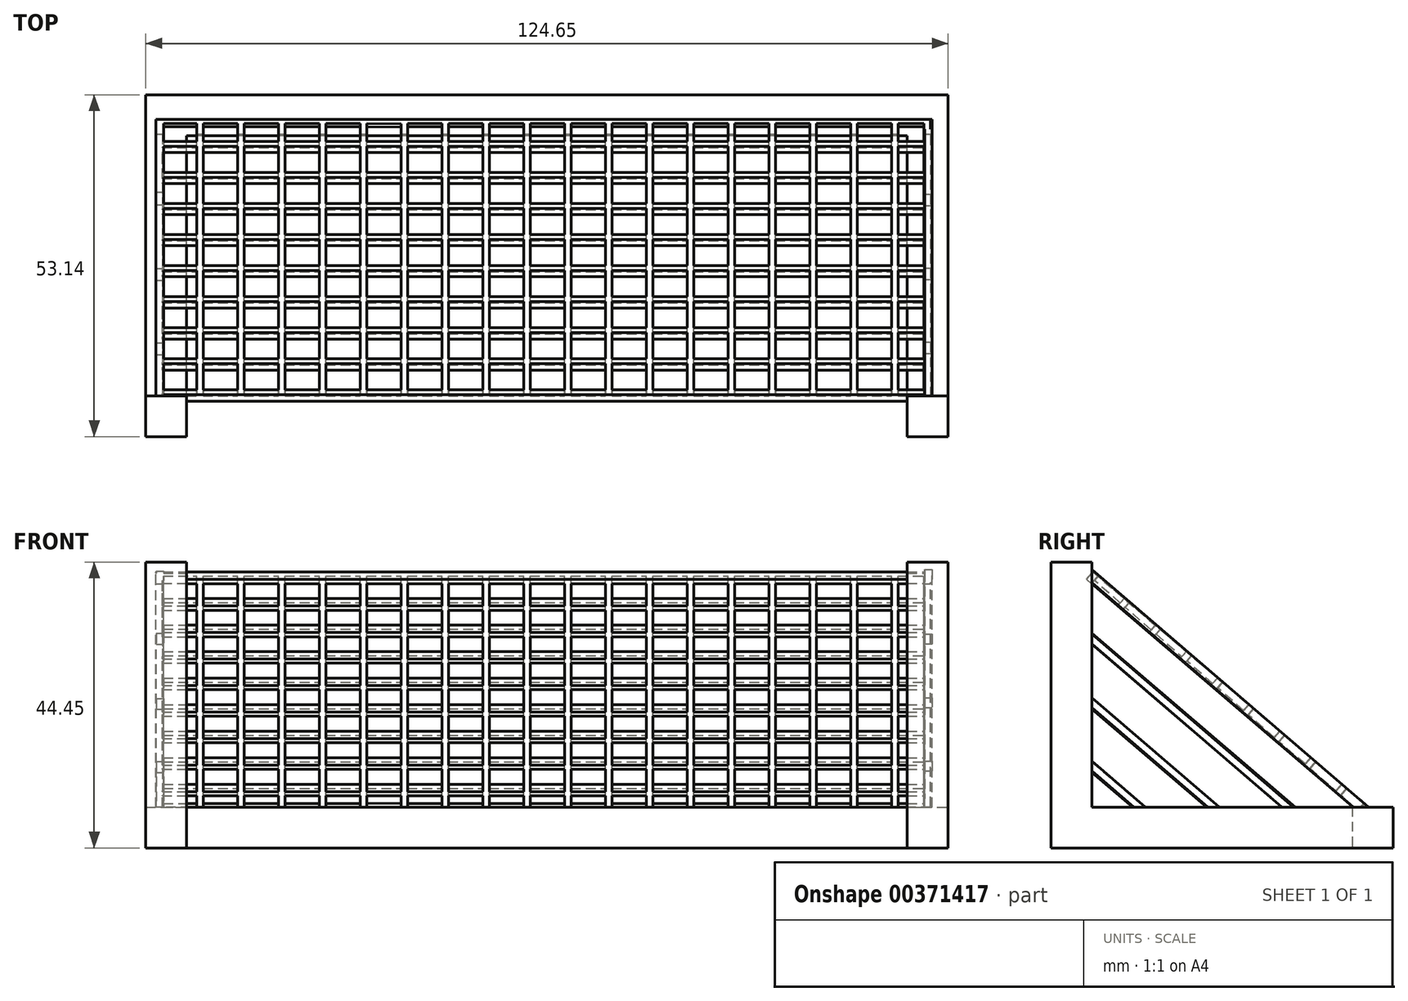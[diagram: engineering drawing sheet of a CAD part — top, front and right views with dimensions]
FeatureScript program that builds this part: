
annotation { "Feature Type Name" : "Feature", "Feature Type Description" : "" }
export const myFeature = defineFeature(function(context is Context, id is Id, definition is map)
    precondition{}
    {
        {
            var Q0;
            Q0=qCreatedBy(makeId("Top.planeOp"),FACE);
            var sketch = newSketch(context, id + "F0", { "sketchPlane" : qUnion([Q0])});
            skLineSegment(sketch, "E0.top", {"start": v(50.52, 38) * mm, "end": v(-74.13, 38) * mm});
            skLineSegment(sketch, "E0.left", {"start": v(50.52, -15.13) * mm, "end": v(50.52, 38) * mm});
            skLineSegment(sketch, "E0.right", {"start": v(-74.13, -15.13) * mm, "end": v(-74.13, 38) * mm});
            skPoint(sketch, "E0.middle", {"position": v(-11.8, 8.26) * mm});
            skLineSegment(sketch, "E1.0", {"start": v(44.17, 31.66) * mm, "end": v(-67.78, 31.66) * mm});
            skLineSegment(sketch, "E1.1", {"start": v(44.17, -15.13) * mm, "end": v(44.17, 31.66) * mm});
            skLineSegment(sketch, "E1.3", {"start": v(-67.78, -15.13) * mm, "end": v(-67.78, 31.66) * mm});
            skLineSegment(sketch, "E2", {"start": v(-74.13, -15.13) * mm, "end": v(-67.78, -15.13) * mm});
            skLineSegment(sketch, "E3", {"start": v(44.17, -15.13) * mm, "end": v(50.52, -15.13) * mm});
            skPoint(sketch, "E4.orphan", {"position": v(-74.13, -21.48) * mm});
            skPoint(sketch, "E5.orphan", {"position": v(50.52, -21.48) * mm});
            skSolve(sketch);
        }
        {
            var Q0;
            Q0=makeQuery(id+"F0.imprint","IMPRINT",FACE,{"disambiguationData":[TD([[makeQuery(id+"F0.imprint","IMPRINT",EDGE,{"derivedFrom":sQuery(id+"F0.wireOp",EDGE,"E0.top")}),1.0]])]});
            extrude(context, id + "F1", {"entities" : qUnion([Q0]), "depth" : 6.35 * mm});
        }
        {
            var Q0;
            Q0=makeQuery(id+"F1.opExtrude","CAP_FACE",FACE,{"disambiguationData":[OSD([sQuery(id+"F0.wireOp",EDGE,"E0.top"),sQuery(id+"F0.wireOp",EDGE,"E0.left"),sQuery(id+"F0.wireOp",EDGE,"E0.right"),sQuery(id+"F0.wireOp",EDGE,"E1.0"),sQuery(id+"F0.wireOp",EDGE,"E1.1"),sQuery(id+"F0.wireOp",EDGE,"E1.3"),sQuery(id+"F0.wireOp",EDGE,"E2"),sQuery(id+"F0.wireOp",EDGE,"E3")])],"isStart":false});
            var sketch = newSketch(context, id + "F2", { "sketchPlane" : qUnion([Q0])});
            skLineSegment(sketch, "E6.bottom", {"start": v(-74.13, -8.78) * mm, "end": v(-67.78, -8.78) * mm});
            skLineSegment(sketch, "E6.top", {"start": v(-74.13, -15.13) * mm, "end": v(-67.78, -15.13) * mm});
            skLineSegment(sketch, "E6.left", {"start": v(-74.13, -8.78) * mm, "end": v(-74.13, -15.13) * mm});
            skLineSegment(sketch, "E6.right", {"start": v(-67.78, -8.78) * mm, "end": v(-67.78, -15.13) * mm});
            skLineSegment(sketch, "E7.bottom", {"start": v(44.17, -8.78) * mm, "end": v(50.52, -8.78) * mm});
            skLineSegment(sketch, "E7.top", {"start": v(44.17, -15.13) * mm, "end": v(50.52, -15.13) * mm});
            skLineSegment(sketch, "E7.left", {"start": v(44.17, -8.78) * mm, "end": v(44.17, -15.13) * mm});
            skLineSegment(sketch, "E7.right", {"start": v(50.52, -8.78) * mm, "end": v(50.52, -15.13) * mm});
            skSolve(sketch);
        }
        {
            var Q0;
            Q0=makeQuery(id+"F2.imprint","IMPRINT",FACE,{"disambiguationData":[TD([[makeQuery(id+"F2.imprint","IMPRINT",EDGE,{"derivedFrom":sQuery(id+"F2.wireOp",EDGE,"E6.bottom")}),-1.0]])]});
            var Q1;
            Q1=makeQuery(id+"F2.imprint","IMPRINT",FACE,{"disambiguationData":[TD([[makeQuery(id+"F2.imprint","IMPRINT",EDGE,{"derivedFrom":sQuery(id+"F2.wireOp",EDGE,"E7.bottom")}),-1.0]])]});
            extrude(context, id + "F3", {"entities" : qUnion([Q0, Q1]), "operationType" : NewBodyOperationType.ADD, "depth" : 38.1 * mm});
        }
        {
            var Q0;
            Q0=qCreatedBy(makeId("Right.planeOp"),FACE);
            cPlane(context, id + "F4", {"entities" : qUnion([Q0]), "cplaneType" : CPlaneType.OFFSET, "offset" : 48 * mm, "width" : 152.4 * mm, "height" : 152.4 * mm});
        }
        {
            var Q0;
            Q0=qCreatedBy(id+"F4.planeOp",FACE);
            var sketch = newSketch(context, id + "F5", { "sketchPlane" : qUnion([Q0])});
            skLineSegment(sketch, "E8.bottom", {"start": v(-9.13, 5.9) * mm, "end": v(34.69, 5.9) * mm});
            skLineSegment(sketch, "E8.left", {"start": v(-9.13, 5.9) * mm, "end": v(-9.13, 43.58) * mm});
            skLineSegment(sketch, "E9", {"start": v(34.69, 5.9) * mm, "end": v(-9.13, 43.58) * mm});
            skLineSegment(sketch, "E10.0", {"start": v(32.74, 5.9) * mm, "end": v(-9.13, 41.91) * mm});
            skLineSegment(sketch, "E11.0", {"start": v(23, 5.9) * mm, "end": v(-9.13, 33.54) * mm});
            skLineSegment(sketch, "E12.0", {"start": v(21.25, 5.9) * mm, "end": v(-9.13, 32.03) * mm});
            skLineSegment(sketch, "E13.0", {"start": v(11.5, 5.9) * mm, "end": v(-9.13, 23.65) * mm});
            skLineSegment(sketch, "E14.0", {"start": v(9.75, 5.9) * mm, "end": v(-9.13, 22.15) * mm});
            skLineSegment(sketch, "E15.0", {"start": v(0.01, 5.9) * mm, "end": v(-9.13, 13.77) * mm});
            skLineSegment(sketch, "E16.0", {"start": v(-1.74, 5.9) * mm, "end": v(-9.13, 12.26) * mm});
            skSolve(sketch);
        }
        {
            var Q0;
            {var subQ0=sQuery(id+"F5.wireOp",EDGE,"E9");Q0=makeQuery(id+"F5.imprint","IMPRINT",FACE,{"disambiguationData":[TD([[makeQuery(id+"F5.imprint","IMPRINT",EDGE,{"derivedFrom":subQ0}),1.0]])]});}
            var Q1;
            {var subQ0=sQuery(id+"F5.wireOp",EDGE,"E11.0");Q1=makeQuery(id+"F5.imprint","IMPRINT",FACE,{"disambiguationData":[TD([[makeQuery(id+"F5.imprint","IMPRINT",EDGE,{"derivedFrom":subQ0}),1.0]])]});}
            var Q2;
            {var subQ0=sQuery(id+"F5.wireOp",EDGE,"E13.0");Q2=makeQuery(id+"F5.imprint","IMPRINT",FACE,{"disambiguationData":[TD([[makeQuery(id+"F5.imprint","IMPRINT",EDGE,{"derivedFrom":subQ0}),1.0]])]});}
            var Q3;
            {var subQ0=sQuery(id+"F5.wireOp",EDGE,"E15.0");Q3=makeQuery(id+"F5.imprint","IMPRINT",FACE,{"disambiguationData":[TD([[makeQuery(id+"F5.imprint","IMPRINT",EDGE,{"derivedFrom":subQ0}),1.0]])]});}
            extrude(context, id + "F6", {"entities" : qUnion([Q0, Q1, Q2, Q3]), "operationType" : NewBodyOperationType.ADD, "oppositeDirection" : true, "depth" : 1.14 * mm});
        }
        {
            var Q0;
            Q0=qCreatedBy(makeId("Right.planeOp"),FACE);
            cPlane(context, id + "F7", {"entities" : qUnion([Q0]), "cplaneType" : CPlaneType.OFFSET, "offset" : 71.37 * mm, "oppositeDirection" : true, "width" : 152.4 * mm, "height" : 152.4 * mm});
        }
        {
            var Q0;
            Q0=qCreatedBy(id+"F7.planeOp",FACE);
            var sketch = newSketch(context, id + "F8", { "sketchPlane" : qUnion([Q0])});
            skLineSegment(sketch, "E17", {"start": v(-9.83, 14.26) * mm, "end": v(0.2, 5.7) * mm});
            skLineSegment(sketch, "E18", {"start": v(11.7, 5.7) * mm, "end": v(-9.62, 23.91) * mm});
            skLineSegment(sketch, "E19", {"start": v(23.6, 5.7) * mm, "end": v(-9.4, 33.88) * mm});
            skLineSegment(sketch, "E20", {"start": v(34.94, 5.7) * mm, "end": v(-9.2, 43.39) * mm});
            skLineSegment(sketch, "E21", {"start": v(21.59, 5.7) * mm, "end": v(-9.44, 32.2) * mm});
            skLineSegment(sketch, "E22", {"start": v(9.83, 5.7) * mm, "end": v(-9.65, 22.34) * mm});
            skLineSegment(sketch, "E23", {"start": v(-1.72, 5.7) * mm, "end": v(-9.86, 12.66) * mm});
            skLineSegment(sketch, "E24", {"start": v(32.72, 5.7) * mm, "end": v(-9.22, 42.3) * mm});
            skLineSegment(sketch, "E25", {"start": v(-8.5, 31.4) * mm, "end": v(-8.5, 33.11) * mm});
            skLineSegment(sketch, "E26", {"start": v(10.97, 6.56) * mm, "end": v(10.7, 6.56) * mm});
            skLineSegment(sketch, "E27", {"start": v(-8.5, 41.67) * mm, "end": v(-8.5, 42.8) * mm});
            skLineSegment(sketch, "E28", {"start": v(37.04, 5.7) * mm, "end": v(-10.01, 5.7) * mm});
            skLineSegment(sketch, "E29", {"start": v(-10.01, 5.7) * mm, "end": v(-9.18, 44.23) * mm});
            skPoint(sketch, "E30.orphan", {"position": v(10.7, 6.56) * mm});
            skPoint(sketch, "E31.end.orphan", {"position": v(20.58, 6.56) * mm});
            skPoint(sketch, "E32.orphan", {"position": v(8.82, 6.56) * mm});
            skPoint(sketch, "E33.end.orphan", {"position": v(-2.73, 6.56) * mm});
            skPoint(sketch, "E34.start.orphan", {"position": v(-8.5, 21.36) * mm});
            skSolve(sketch);
        }
        {
            var Q0;
            Q0=makeQuery(id+"F8.imprint","IMPRINT",FACE,{"disambiguationData":[TD([[makeQuery(id+"F8.imprint","IMPRINT",EDGE,{"derivedFrom":sQuery(id+"F8.wireOp",EDGE,"E17")}),-1.0]])]});
            var Q1;
            Q1=makeQuery(id+"F8.imprint","IMPRINT",FACE,{"disambiguationData":[TD([[makeQuery(id+"F8.imprint","IMPRINT",EDGE,{"derivedFrom":sQuery(id+"F8.wireOp",EDGE,"E18")}),1.0]])]});
            var Q2;
            Q2=makeQuery(id+"F8.imprint","IMPRINT",FACE,{"disambiguationData":[TD([[makeQuery(id+"F8.imprint","IMPRINT",EDGE,{"derivedFrom":sQuery(id+"F8.wireOp",EDGE,"E19")}),1.0]])]});
            var Q3;
            Q3=makeQuery(id+"F8.imprint","IMPRINT",FACE,{"disambiguationData":[TD([[makeQuery(id+"F8.imprint","IMPRINT",EDGE,{"derivedFrom":sQuery(id+"F8.wireOp",EDGE,"E20")}),1.0]])]});
            extrude(context, id + "F9", {"entities" : qUnion([Q0, Q1, Q2, Q3]), "operationType" : NewBodyOperationType.ADD, "oppositeDirection" : true, "depth" : 1.14 * mm});
        }
        {
            var Q0;
            Q0=makeQuery(id+"F9.opExtrude","SWEPT_FACE",FACE,{"disambiguationData":[OSD([sQuery(id+"F8.wireOp",EDGE,"E20")])]});
            cPlane(context, id + "F10", {"entities" : qUnion([Q0]), "cplaneType" : CPlaneType.OFFSET, "offset" : 0 * mm, "width" : 152.4 * mm, "height" : 152.4 * mm});
        }
        {
            var Q0;
            Q0=qCreatedBy(id+"F10.planeOp",FACE);
            var sketch = newSketch(context, id + "F11", { "sketchPlane" : qUnion([Q0])});
            skLineSegment(sketch, "E35.bottom", {"start": v(-72.57, 22.01) * mm, "end": v(47.8, 22.01) * mm});
            skLineSegment(sketch, "E35.top", {"start": v(-72.57, -34.41) * mm, "end": v(47.8, -34.41) * mm});
            skLineSegment(sketch, "E35.left", {"start": v(-72.57, 22.01) * mm, "end": v(-72.57, -34.41) * mm});
            skLineSegment(sketch, "E35.right", {"start": v(47.8, 22.01) * mm, "end": v(47.8, -34.41) * mm});
            skLineSegment(sketch, "E36.0", {"start": v(-71.56, 21) * mm, "end": v(-66.22, 21) * mm});
            skLineSegment(sketch, "E36.1", {"start": v(-71.56, 21) * mm, "end": v(-71.56, 16.39) * mm});
            skLineSegment(sketch, "E36.2", {"start": v(-71.56, -33.4) * mm, "end": v(-40.82, -33.4) * mm});
            skLineSegment(sketch, "E36.3", {"start": v(46.78, 21) * mm, "end": v(46.78, -8) * mm});
            skLineSegment(sketch, "E37.0", {"start": v(-66.22, 22.01) * mm, "end": v(-66.22, 21) * mm});
            skLineSegment(sketch, "E38.0.1.0", {"start": v(-65.2, 22.26) * mm, "end": v(-65.2, 22.01) * mm});
            skLineSegment(sketch, "E38.0.1.1", {"start": v(-66.22, 22.26) * mm, "end": v(-66.22, 22.01) * mm});
            skLineSegment(sketch, "E38.1.0.0", {"start": v(-58.86, 21) * mm, "end": v(-58.86, 17.4) * mm});
            skLineSegment(sketch, "E38.1.0.1", {"start": v(-59.87, 22.01) * mm, "end": v(-59.87, -2.66) * mm});
            skLineSegment(sketch, "E38.1.1.0", {"start": v(-58.86, 22.26) * mm, "end": v(-58.86, 22.01) * mm});
            skLineSegment(sketch, "E38.1.1.1", {"start": v(-59.87, 22.26) * mm, "end": v(-59.87, 10.04) * mm});
            skLineSegment(sketch, "E38.2.0.0", {"start": v(-52.5, 21) * mm, "end": v(-52.5, 17.4) * mm});
            skLineSegment(sketch, "E38.2.0.1", {"start": v(-53.52, 22.01) * mm, "end": v(-53.52, 10.04) * mm});
            skLineSegment(sketch, "E38.2.1.0", {"start": v(-52.5, 22.26) * mm, "end": v(-52.5, 22.01) * mm});
            skLineSegment(sketch, "E38.2.1.1", {"start": v(-53.52, 22.26) * mm, "end": v(-53.52, 10.04) * mm});
            skLineSegment(sketch, "E38.3.0.0", {"start": v(-46.16, 21) * mm, "end": v(-46.16, 17.4) * mm});
            skLineSegment(sketch, "E38.3.0.1", {"start": v(-47.17, 22.01) * mm, "end": v(-47.17, 4.7) * mm});
            skLineSegment(sketch, "E38.3.1.1", {"start": v(-47.17, 22.26) * mm, "end": v(-47.17, 10.04) * mm});
            skLineSegment(sketch, "E38.4.0.1", {"start": v(-40.82, 22.01) * mm, "end": v(-40.82, 4.7) * mm});
            skLineSegment(sketch, "E38.4.1.1", {"start": v(-40.82, 22.26) * mm, "end": v(-40.82, 17.4) * mm});
            skLineSegment(sketch, "E38.5.0.1", {"start": v(-34.47, 22.01) * mm, "end": v(-34.47, 11.05) * mm});
            skLineSegment(sketch, "E38.5.1.1", {"start": v(-34.47, 22.26) * mm, "end": v(-34.47, 4.7) * mm});
            skLineSegment(sketch, "E38.6.0.1", {"start": v(-28.12, 17.4) * mm, "end": v(-28.12, 10.04) * mm});
            skLineSegment(sketch, "E38.6.1.0", {"start": v(-27.1, 22.26) * mm, "end": v(-27.1, 22.01) * mm});
            skLineSegment(sketch, "E38.7.0.1", {"start": v(-21.77, 22.01) * mm, "end": v(-21.77, 10.04) * mm});
            skLineSegment(sketch, "E38.7.1.1", {"start": v(-21.77, 22.26) * mm, "end": v(-21.77, 10.04) * mm});
            skLineSegment(sketch, "E38.8.0.1", {"start": v(-15.42, 22.01) * mm, "end": v(-15.42, 4.7) * mm});
            skLineSegment(sketch, "E38.8.1.1", {"start": v(-15.42, 22.26) * mm, "end": v(-15.42, 17.4) * mm});
            skLineSegment(sketch, "E38.9.0.0", {"start": v(-8.06, 21) * mm, "end": v(-8.06, 17.4) * mm});
            skLineSegment(sketch, "E38.9.0.1", {"start": v(-9.07, 22.01) * mm, "end": v(-9.07, 4.7) * mm});
            skLineSegment(sketch, "E38.9.1.0", {"start": v(-8.06, 22.26) * mm, "end": v(-8.06, 22.01) * mm});
            skLineSegment(sketch, "E38.9.1.1", {"start": v(-9.07, 22.26) * mm, "end": v(-9.07, 17.4) * mm});
            skLineSegment(sketch, "E38.10.0.1", {"start": v(-2.72, 22.01) * mm, "end": v(-2.72, 4.7) * mm});
            skLineSegment(sketch, "E38.10.1.0", {"start": v(-1.7, 22.26) * mm, "end": v(-1.7, 22.01) * mm});
            skLineSegment(sketch, "E38.10.1.1", {"start": v(-2.72, 22.26) * mm, "end": v(-2.72, 4.7) * mm});
            skLineSegment(sketch, "E38.11.0.0", {"start": v(4.64, 21) * mm, "end": v(4.64, 17.4) * mm});
            skLineSegment(sketch, "E38.11.0.1", {"start": v(3.63, 22.01) * mm, "end": v(3.63, 4.7) * mm});
            skLineSegment(sketch, "E38.11.1.0", {"start": v(4.64, 22.26) * mm, "end": v(4.64, 22.01) * mm});
            skLineSegment(sketch, "E38.11.1.1", {"start": v(3.63, 22.26) * mm, "end": v(3.63, 4.7) * mm});
            skLineSegment(sketch, "E38.12.0.0", {"start": v(11, 21) * mm, "end": v(11, 17.4) * mm});
            skLineSegment(sketch, "E38.12.0.1", {"start": v(9.98, 22.01) * mm, "end": v(9.98, 4.7) * mm});
            skLineSegment(sketch, "E38.12.1.0", {"start": v(11, 22.26) * mm, "end": v(11, 22.01) * mm});
            skLineSegment(sketch, "E38.12.1.1", {"start": v(9.98, 22.26) * mm, "end": v(9.98, 11.05) * mm});
            skLineSegment(sketch, "E38.13.0.0", {"start": v(17.34, 21) * mm, "end": v(17.34, 17.4) * mm});
            skLineSegment(sketch, "E38.13.0.1", {"start": v(16.33, 22.01) * mm, "end": v(16.33, 11.05) * mm});
            skLineSegment(sketch, "E38.13.1.0", {"start": v(17.34, 22.26) * mm, "end": v(17.34, 22.01) * mm});
            skLineSegment(sketch, "E38.13.1.1", {"start": v(16.33, 22.26) * mm, "end": v(16.33, 11.05) * mm});
            skLineSegment(sketch, "E38.14.0.0", {"start": v(23.7, 21) * mm, "end": v(23.7, 17.4) * mm});
            skLineSegment(sketch, "E38.14.0.1", {"start": v(22.68, 22.01) * mm, "end": v(22.68, 11.05) * mm});
            skLineSegment(sketch, "E38.14.1.0", {"start": v(23.7, 22.26) * mm, "end": v(23.7, 22.01) * mm});
            skLineSegment(sketch, "E38.14.1.1", {"start": v(22.68, 22.26) * mm, "end": v(22.68, 11.05) * mm});
            skLineSegment(sketch, "E38.15.0.0", {"start": v(30.04, 21) * mm, "end": v(30.04, 17.4) * mm});
            skLineSegment(sketch, "E38.15.0.1", {"start": v(29.03, 22.01) * mm, "end": v(29.03, 11.05) * mm});
            skLineSegment(sketch, "E38.15.1.0", {"start": v(30.04, 22.26) * mm, "end": v(30.04, 22.01) * mm});
            skLineSegment(sketch, "E38.15.1.1", {"start": v(29.03, 22.26) * mm, "end": v(29.03, 11.05) * mm});
            skLineSegment(sketch, "E38.16.0.0", {"start": v(36.4, 21) * mm, "end": v(36.4, 17.4) * mm});
            skLineSegment(sketch, "E38.16.0.1", {"start": v(35.38, 22.01) * mm, "end": v(35.38, 11.05) * mm});
            skLineSegment(sketch, "E38.16.1.0", {"start": v(36.4, 22.26) * mm, "end": v(36.4, 22.01) * mm});
            skLineSegment(sketch, "E38.16.1.1", {"start": v(35.38, 22.26) * mm, "end": v(35.38, 16.39) * mm});
            skLineSegment(sketch, "E38.17.0.0", {"start": v(42.74, 21) * mm, "end": v(42.74, 17.4) * mm});
            skLineSegment(sketch, "E38.17.0.1", {"start": v(41.73, 22.01) * mm, "end": v(41.73, 11.05) * mm});
            skLineSegment(sketch, "E38.17.1.0", {"start": v(42.74, 22.26) * mm, "end": v(42.74, 22.01) * mm});
            skLineSegment(sketch, "E38.17.1.1", {"start": v(41.73, 22.26) * mm, "end": v(41.73, 16.39) * mm});
            skLineSegment(sketch, "E38.direction1", {"start": v(-66.22, -34.41) * mm, "end": v(-59.87, -34.41) * mm, "construction": true});
            skLineSegment(sketch, "E39.0.1.0", {"start": v(-71.56, -28.06) * mm, "end": v(-66.22, -28.06) * mm});
            skLineSegment(sketch, "E39.0.1.1", {"start": v(-71.56, -27.05) * mm, "end": v(-66.22, -27.05) * mm});
            skLineSegment(sketch, "E39.0.2.0", {"start": v(-71.56, -21.71) * mm, "end": v(-66.22, -21.71) * mm});
            skLineSegment(sketch, "E39.0.2.1", {"start": v(-71.56, -20.7) * mm, "end": v(-66.22, -20.7) * mm});
            skLineSegment(sketch, "E39.0.3.1", {"start": v(-71.56, -14.35) * mm, "end": v(-66.22, -14.35) * mm});
            skLineSegment(sketch, "E39.0.4.0", {"start": v(-72.57, -9.01) * mm, "end": v(-66.22, -9.01) * mm});
            skLineSegment(sketch, "E39.0.4.1", {"start": v(-71.56, -8) * mm, "end": v(-66.22, -8) * mm});
            skLineSegment(sketch, "E39.0.5.0", {"start": v(-71.56, -2.66) * mm, "end": v(-66.22, -2.66) * mm});
            skLineSegment(sketch, "E39.0.5.1", {"start": v(-71.56, -1.65) * mm, "end": v(-66.22, -1.65) * mm});
            skLineSegment(sketch, "E39.0.6.0", {"start": v(-71.56, 3.69) * mm, "end": v(-66.22, 3.69) * mm});
            skLineSegment(sketch, "E39.0.6.1", {"start": v(-71.56, 4.7) * mm, "end": v(-66.22, 4.7) * mm});
            skLineSegment(sketch, "E39.0.7.1", {"start": v(-71.56, 11.05) * mm, "end": v(-66.22, 11.05) * mm});
            skLineSegment(sketch, "E39.0.8.0", {"start": v(-71.56, 16.39) * mm, "end": v(-66.22, 16.39) * mm});
            skLineSegment(sketch, "E39.0.8.1", {"start": v(-71.56, 17.4) * mm, "end": v(-66.22, 17.4) * mm});
            skLineSegment(sketch, "E39.1.0.0", {"start": v(-72.83, -34.41) * mm, "end": v(47.55, -34.41) * mm});
            skLineSegment(sketch, "E39.1.0.1", {"start": v(-71.81, -33.4) * mm, "end": v(-59.87, -33.4) * mm});
            skLineSegment(sketch, "E39.1.1.0", {"start": v(-72.83, -28.06) * mm, "end": v(-72.57, -28.06) * mm});
            skLineSegment(sketch, "E39.1.1.1", {"start": v(-71.81, -27.05) * mm, "end": v(-66.22, -27.05) * mm});
            skLineSegment(sketch, "E39.1.2.0", {"start": v(-72.83, -21.71) * mm, "end": v(-72.57, -21.71) * mm});
            skLineSegment(sketch, "E39.1.2.1", {"start": v(-71.81, -20.7) * mm, "end": v(-66.22, -20.7) * mm});
            skLineSegment(sketch, "E39.1.3.0", {"start": v(-72.83, -15.36) * mm, "end": v(-72.57, -15.36) * mm});
            skLineSegment(sketch, "E39.1.3.1", {"start": v(-71.81, -14.35) * mm, "end": v(-66.22, -14.35) * mm});
            skLineSegment(sketch, "E39.1.4.0", {"start": v(-72.83, -9.01) * mm, "end": v(-66.22, -9.01) * mm});
            skLineSegment(sketch, "E39.1.4.1", {"start": v(-71.81, -8) * mm, "end": v(-66.22, -8) * mm});
            skLineSegment(sketch, "E39.1.5.0", {"start": v(-72.83, -2.66) * mm, "end": v(-72.57, -2.66) * mm});
            skLineSegment(sketch, "E39.1.5.1", {"start": v(-71.81, -1.65) * mm, "end": v(-66.22, -1.65) * mm});
            skLineSegment(sketch, "E39.1.6.1", {"start": v(-71.81, 4.7) * mm, "end": v(-66.22, 4.7) * mm});
            skLineSegment(sketch, "E39.1.7.0", {"start": v(-72.83, 10.04) * mm, "end": v(-72.57, 10.04) * mm});
            skLineSegment(sketch, "E39.1.7.1", {"start": v(-71.81, 11.05) * mm, "end": v(-66.22, 11.05) * mm});
            skLineSegment(sketch, "E39.1.8.0", {"start": v(-72.83, 16.39) * mm, "end": v(-72.57, 16.39) * mm});
            skLineSegment(sketch, "E39.1.8.1", {"start": v(-71.81, 17.4) * mm, "end": v(-66.22, 17.4) * mm});
            skLineSegment(sketch, "E39.2.0.0", {"start": v(-73.08, -34.41) * mm, "end": v(4.64, -34.41) * mm});
            skLineSegment(sketch, "E39.2.0.1", {"start": v(-72.07, -33.4) * mm, "end": v(-53.52, -33.4) * mm});
            skLineSegment(sketch, "E39.2.1.0", {"start": v(-73.08, -28.06) * mm, "end": v(-72.57, -28.06) * mm});
            skLineSegment(sketch, "E39.2.1.1", {"start": v(-72.07, -27.05) * mm, "end": v(-66.22, -27.05) * mm});
            skLineSegment(sketch, "E39.2.2.0", {"start": v(-73.08, -21.71) * mm, "end": v(-72.57, -21.71) * mm});
            skLineSegment(sketch, "E39.2.2.1", {"start": v(-72.07, -20.7) * mm, "end": v(-66.22, -20.7) * mm});
            skLineSegment(sketch, "E39.2.3.0", {"start": v(-73.08, -15.36) * mm, "end": v(-72.57, -15.36) * mm});
            skLineSegment(sketch, "E39.2.3.1", {"start": v(-72.07, -14.35) * mm, "end": v(-66.22, -14.35) * mm});
            skLineSegment(sketch, "E39.2.4.0", {"start": v(-73.08, -9.01) * mm, "end": v(-66.22, -9.01) * mm});
            skLineSegment(sketch, "E39.2.4.1", {"start": v(-72.07, -8) * mm, "end": v(-66.22, -8) * mm});
            skLineSegment(sketch, "E39.2.5.0", {"start": v(-73.08, -2.66) * mm, "end": v(-72.83, -2.66) * mm});
            skLineSegment(sketch, "E39.2.5.1", {"start": v(-72.07, -1.65) * mm, "end": v(-66.22, -1.65) * mm});
            skLineSegment(sketch, "E39.2.6.0", {"start": v(-73.08, 3.69) * mm, "end": v(-72.83, 3.69) * mm});
            skLineSegment(sketch, "E39.2.6.1", {"start": v(-72.07, 4.7) * mm, "end": v(-66.22, 4.7) * mm});
            skLineSegment(sketch, "E39.2.7.0", {"start": v(-73.08, 10.04) * mm, "end": v(-72.57, 10.04) * mm});
            skLineSegment(sketch, "E39.2.7.1", {"start": v(-72.07, 11.05) * mm, "end": v(-66.22, 11.05) * mm});
            skLineSegment(sketch, "E39.2.8.0", {"start": v(-73.08, 16.39) * mm, "end": v(-72.57, 16.39) * mm});
            skLineSegment(sketch, "E39.2.8.1", {"start": v(-72.07, 17.4) * mm, "end": v(-66.22, 17.4) * mm});
            skLineSegment(sketch, "E39.direction1", {"start": v(-72.57, -34.41) * mm, "end": v(-72.83, -34.41) * mm, "construction": true});
            skLineSegment(sketch, "E39.direction2", {"start": v(-72.57, -34.41) * mm, "end": v(-72.57, -28.06) * mm, "construction": true});
            skLineSegment(sketch, "E40.trimOffspring", {"start": v(-1.7, -9.01) * mm, "end": v(3.63, -9.01) * mm});
            skLineSegment(sketch, "E41.trimOffspring", {"start": v(-1.7, -9.01) * mm, "end": v(-1.7, -14.35) * mm});
            skLineSegment(sketch, "E42.trimOffspring", {"start": v(-2.72, -9.01) * mm, "end": v(-2.72, -14.35) * mm});
            skLineSegment(sketch, "E43.trimOffspring", {"start": v(-1.7, -8) * mm, "end": v(3.63, -8) * mm});
            skLineSegment(sketch, "E44.trimOffspring", {"start": v(-1.7, -14.35) * mm, "end": v(3.63, -14.35) * mm});
            skLineSegment(sketch, "E45.trimOffspring", {"start": v(-1.7, -15.36) * mm, "end": v(-1.7, -20.7) * mm});
            skLineSegment(sketch, "E46.trimOffspring", {"start": v(-1.7, -15.36) * mm, "end": v(3.63, -15.36) * mm});
            skLineSegment(sketch, "E47.trimOffspring", {"start": v(-2.72, -15.36) * mm, "end": v(-2.72, -34.16) * mm});
            skLineSegment(sketch, "E48.trimOffspring", {"start": v(9.98, -15.36) * mm, "end": v(9.98, -34.16) * mm});
            skLineSegment(sketch, "E49.trimOffspring", {"start": v(11, -15.36) * mm, "end": v(16.33, -15.36) * mm});
            skLineSegment(sketch, "E50.trimOffspring", {"start": v(11, -15.36) * mm, "end": v(11, -20.7) * mm});
            skLineSegment(sketch, "E51.trimOffspring", {"start": v(11, -14.35) * mm, "end": v(16.33, -14.35) * mm});
            skLineSegment(sketch, "E52.trimOffspring", {"start": v(16.33, -15.36) * mm, "end": v(16.33, -34.16) * mm});
            skLineSegment(sketch, "E53.trimOffspring", {"start": v(17.34, -15.36) * mm, "end": v(22.68, -15.36) * mm});
            skLineSegment(sketch, "E54.trimOffspring", {"start": v(-33.46, -33.4) * mm, "end": v(-28.12, -33.4) * mm});
            skLineSegment(sketch, "E55.trimOffspring", {"start": v(-33.46, -34.16) * mm, "end": v(-33.46, -34.41) * mm});
            skPoint(sketch, "E56.orphan", {"position": v(-34.47, -34.16) * mm});
            skLineSegment(sketch, "E57.trimOffspring", {"start": v(-34.47, -28.06) * mm, "end": v(-34.47, -33.4) * mm});
            skLineSegment(sketch, "E58.trimOffspring", {"start": v(-33.46, -28.06) * mm, "end": v(-33.46, -33.4) * mm});
            skLineSegment(sketch, "E59.trimOffspring", {"start": v(-33.46, -28.06) * mm, "end": v(-28.12, -28.06) * mm});
            skLineSegment(sketch, "E60.trimOffspring", {"start": v(-33.46, -27.05) * mm, "end": v(-28.12, -27.05) * mm});
            skLineSegment(sketch, "E61.trimOffspring", {"start": v(-27.1, -27.05) * mm, "end": v(-21.77, -27.05) * mm});
            skLineSegment(sketch, "E62.trimOffspring", {"start": v(-27.1, -28.06) * mm, "end": v(-21.77, -28.06) * mm});
            skLineSegment(sketch, "E63.trimOffspring", {"start": v(-20.76, -28.06) * mm, "end": v(-15.42, -28.06) * mm});
            skLineSegment(sketch, "E64.trimOffspring", {"start": v(-20.76, -27.05) * mm, "end": v(-15.42, -27.05) * mm});
            skLineSegment(sketch, "E65.trimOffspring", {"start": v(-14.4, -28.06) * mm, "end": v(-9.07, -28.06) * mm});
            skLineSegment(sketch, "E66.trimOffspring", {"start": v(-14.4, -27.05) * mm, "end": v(-9.07, -27.05) * mm});
            skLineSegment(sketch, "E67.trimOffspring", {"start": v(-8.06, -28.06) * mm, "end": v(-2.72, -28.06) * mm});
            skLineSegment(sketch, "E68.trimOffspring", {"start": v(-8.06, -27.05) * mm, "end": v(-2.72, -27.05) * mm});
            skLineSegment(sketch, "E69.trimOffspring", {"start": v(-1.7, -27.05) * mm, "end": v(3.63, -27.05) * mm});
            skLineSegment(sketch, "E70.trimOffspring", {"start": v(-1.7, -28.06) * mm, "end": v(3.63, -28.06) * mm});
            skLineSegment(sketch, "E71.trimOffspring", {"start": v(4.64, -28.06) * mm, "end": v(9.98, -28.06) * mm});
            skLineSegment(sketch, "E72.trimOffspring", {"start": v(4.64, -27.05) * mm, "end": v(9.98, -27.05) * mm});
            skLineSegment(sketch, "E73.trimOffspring", {"start": v(11, -28.06) * mm, "end": v(16.33, -28.06) * mm});
            skLineSegment(sketch, "E74.trimOffspring", {"start": v(11, -27.05) * mm, "end": v(16.33, -27.05) * mm});
            skLineSegment(sketch, "E75.trimOffspring", {"start": v(17.34, -28.06) * mm, "end": v(22.68, -28.06) * mm});
            skLineSegment(sketch, "E76.trimOffspring", {"start": v(17.34, -27.05) * mm, "end": v(22.68, -27.05) * mm});
            skLineSegment(sketch, "E77.trimOffspring", {"start": v(23.7, -28.06) * mm, "end": v(29.03, -28.06) * mm});
            skLineSegment(sketch, "E78.trimOffspring", {"start": v(23.7, -27.05) * mm, "end": v(29.03, -27.05) * mm});
            skLineSegment(sketch, "E79.trimOffspring", {"start": v(30.04, -28.06) * mm, "end": v(35.38, -28.06) * mm});
            skLineSegment(sketch, "E80.trimOffspring", {"start": v(30.04, -27.05) * mm, "end": v(35.38, -27.05) * mm});
            skLineSegment(sketch, "E81.trimOffspring", {"start": v(36.4, -28.06) * mm, "end": v(41.73, -28.06) * mm});
            skLineSegment(sketch, "E82.trimOffspring", {"start": v(42.74, -28.06) * mm, "end": v(47.3, -28.06) * mm});
            skLineSegment(sketch, "E83.trimOffspring", {"start": v(42.74, -28.06) * mm, "end": v(47.55, -28.06) * mm});
            skLineSegment(sketch, "E84.trimOffspring", {"start": v(42.74, -28.06) * mm, "end": v(46.78, -28.06) * mm});
            skLineSegment(sketch, "E85.trimOffspring", {"start": v(42.74, -27.05) * mm, "end": v(46.53, -27.05) * mm});
            skLineSegment(sketch, "E86.trimOffspring", {"start": v(42.74, -27.05) * mm, "end": v(46.78, -27.05) * mm});
            skLineSegment(sketch, "E87.trimOffspring", {"start": v(42.74, -27.05) * mm, "end": v(46.28, -27.05) * mm});
            skLineSegment(sketch, "E88", {"start": v(36.4, -27.05) * mm, "end": v(41.73, -27.05) * mm});
            skLineSegment(sketch, "E89.trimOffspring", {"start": v(42.74, -21.71) * mm, "end": v(47.3, -21.71) * mm});
            skLineSegment(sketch, "E90.trimOffspring", {"start": v(42.74, -21.71) * mm, "end": v(47.55, -21.71) * mm});
            skLineSegment(sketch, "E91.trimOffspring", {"start": v(42.74, -20.7) * mm, "end": v(46.28, -20.7) * mm});
            skLineSegment(sketch, "E92.trimOffspring", {"start": v(42.74, -20.7) * mm, "end": v(46.53, -20.7) * mm});
            skLineSegment(sketch, "E93.trimOffspring", {"start": v(42.74, -20.7) * mm, "end": v(46.78, -20.7) * mm});
            skLineSegment(sketch, "E94.trimOffspring", {"start": v(36.4, -20.7) * mm, "end": v(41.73, -20.7) * mm});
            skLineSegment(sketch, "E95.trimOffspring", {"start": v(36.4, -21.71) * mm, "end": v(41.73, -21.71) * mm});
            skLineSegment(sketch, "E96.trimOffspring", {"start": v(30.04, -21.71) * mm, "end": v(35.38, -21.71) * mm});
            skLineSegment(sketch, "E97.trimOffspring", {"start": v(30.04, -20.7) * mm, "end": v(35.38, -20.7) * mm});
            skLineSegment(sketch, "E98.trimOffspring", {"start": v(30.04, -15.36) * mm, "end": v(35.38, -15.36) * mm});
            skLineSegment(sketch, "E99.trimOffspring", {"start": v(30.04, -14.35) * mm, "end": v(35.38, -14.35) * mm});
            skLineSegment(sketch, "E100.trimOffspring", {"start": v(36.4, -15.36) * mm, "end": v(41.73, -15.36) * mm});
            skLineSegment(sketch, "E101.trimOffspring", {"start": v(36.4, -14.35) * mm, "end": v(41.73, -14.35) * mm});
            skLineSegment(sketch, "E102.trimOffspring", {"start": v(42.74, -15.36) * mm, "end": v(47.55, -15.36) * mm});
            skLineSegment(sketch, "E103.trimOffspring", {"start": v(42.74, -15.36) * mm, "end": v(47.3, -15.36) * mm});
            skLineSegment(sketch, "E104.trimOffspring", {"start": v(42.74, -14.35) * mm, "end": v(46.78, -14.35) * mm});
            skLineSegment(sketch, "E105.trimOffspring", {"start": v(42.74, -14.35) * mm, "end": v(46.28, -14.35) * mm});
            skLineSegment(sketch, "E106.trimOffspring", {"start": v(42.74, -14.35) * mm, "end": v(46.53, -14.35) * mm});
            skLineSegment(sketch, "E107.trimOffspring", {"start": v(23.7, -15.36) * mm, "end": v(29.03, -15.36) * mm});
            skLineSegment(sketch, "E108.trimOffspring", {"start": v(23.7, -14.35) * mm, "end": v(29.03, -14.35) * mm});
            skLineSegment(sketch, "E109.trimOffspring", {"start": v(23.7, -20.7) * mm, "end": v(29.03, -20.7) * mm});
            skLineSegment(sketch, "E110.trimOffspring", {"start": v(23.7, -21.71) * mm, "end": v(29.03, -21.71) * mm});
            skLineSegment(sketch, "E111.trimOffspring", {"start": v(17.34, -21.71) * mm, "end": v(22.68, -21.71) * mm});
            skLineSegment(sketch, "E112.trimOffspring", {"start": v(17.34, -20.7) * mm, "end": v(22.68, -20.7) * mm});
            skLineSegment(sketch, "E113.trimOffspring", {"start": v(17.34, -14.35) * mm, "end": v(22.68, -14.35) * mm});
            skLineSegment(sketch, "E114.trimOffspring", {"start": v(11, -20.7) * mm, "end": v(16.33, -20.7) * mm});
            skLineSegment(sketch, "E115.trimOffspring", {"start": v(11, -21.71) * mm, "end": v(16.33, -21.71) * mm});
            skLineSegment(sketch, "E116.trimOffspring", {"start": v(4.64, -21.71) * mm, "end": v(9.98, -21.71) * mm});
            skLineSegment(sketch, "E117.trimOffspring", {"start": v(4.64, -20.7) * mm, "end": v(9.98, -20.7) * mm});
            skLineSegment(sketch, "E118.trimOffspring", {"start": v(4.64, -14.35) * mm, "end": v(9.98, -14.35) * mm});
            skLineSegment(sketch, "E119.trimOffspring", {"start": v(4.64, -15.36) * mm, "end": v(9.98, -15.36) * mm});
            skLineSegment(sketch, "E120.trimOffspring", {"start": v(-1.7, -20.7) * mm, "end": v(3.63, -20.7) * mm});
            skLineSegment(sketch, "E121.trimOffspring", {"start": v(-1.7, -21.71) * mm, "end": v(3.63, -21.71) * mm});
            skLineSegment(sketch, "E122.trimOffspring", {"start": v(-8.06, -14.35) * mm, "end": v(-2.72, -14.35) * mm});
            skLineSegment(sketch, "E123.trimOffspring", {"start": v(-8.06, -15.36) * mm, "end": v(-2.72, -15.36) * mm});
            skLineSegment(sketch, "E124.trimOffspring", {"start": v(-8.06, -20.7) * mm, "end": v(-2.72, -20.7) * mm});
            skLineSegment(sketch, "E125.trimOffspring", {"start": v(-8.06, -21.71) * mm, "end": v(-2.72, -21.71) * mm});
            skLineSegment(sketch, "E126.trimOffspring", {"start": v(-14.4, -15.36) * mm, "end": v(-9.07, -15.36) * mm});
            skLineSegment(sketch, "E127.trimOffspring", {"start": v(-14.4, -14.35) * mm, "end": v(-9.07, -14.35) * mm});
            skLineSegment(sketch, "E128.trimOffspring", {"start": v(-14.4, -20.7) * mm, "end": v(-9.07, -20.7) * mm});
            skLineSegment(sketch, "E129.trimOffspring", {"start": v(-14.4, -21.71) * mm, "end": v(-9.07, -21.71) * mm});
            skLineSegment(sketch, "E130.trimOffspring", {"start": v(-20.76, -21.71) * mm, "end": v(-15.42, -21.71) * mm});
            skLineSegment(sketch, "E131.trimOffspring", {"start": v(-20.76, -20.7) * mm, "end": v(-15.42, -20.7) * mm});
            skLineSegment(sketch, "E132.trimOffspring", {"start": v(-20.76, -15.36) * mm, "end": v(-15.42, -15.36) * mm});
            skLineSegment(sketch, "E133.trimOffspring", {"start": v(-20.76, -14.35) * mm, "end": v(-15.42, -14.35) * mm});
            skLineSegment(sketch, "E134.trimOffspring", {"start": v(-27.1, -14.35) * mm, "end": v(-21.77, -14.35) * mm});
            skLineSegment(sketch, "E135.trimOffspring", {"start": v(-27.1, -15.36) * mm, "end": v(-21.77, -15.36) * mm});
            skLineSegment(sketch, "E136.trimOffspring", {"start": v(-27.1, -20.7) * mm, "end": v(-21.77, -20.7) * mm});
            skLineSegment(sketch, "E137.trimOffspring", {"start": v(-27.1, -21.71) * mm, "end": v(-21.77, -21.71) * mm});
            skLineSegment(sketch, "E138.trimOffspring", {"start": v(-33.46, -21.71) * mm, "end": v(-28.12, -21.71) * mm});
            skLineSegment(sketch, "E139.trimOffspring", {"start": v(-33.46, -20.7) * mm, "end": v(-28.12, -20.7) * mm});
            skLineSegment(sketch, "E140.trimOffspring", {"start": v(-33.46, -15.36) * mm, "end": v(-28.12, -15.36) * mm});
            skLineSegment(sketch, "E141.trimOffspring", {"start": v(-33.46, -14.35) * mm, "end": v(-28.12, -14.35) * mm});
            skLineSegment(sketch, "E142.trimOffspring", {"start": v(-39.8, -14.35) * mm, "end": v(-34.47, -14.35) * mm});
            skLineSegment(sketch, "E143.trimOffspring", {"start": v(-39.8, -15.36) * mm, "end": v(-34.47, -15.36) * mm});
            skLineSegment(sketch, "E144.trimOffspring", {"start": v(-39.8, -20.7) * mm, "end": v(-34.47, -20.7) * mm});
            skLineSegment(sketch, "E145.trimOffspring", {"start": v(-39.8, -21.71) * mm, "end": v(-34.47, -21.71) * mm});
            skLineSegment(sketch, "E146.trimOffspring", {"start": v(-46.16, -28.06) * mm, "end": v(-40.82, -28.06) * mm});
            skLineSegment(sketch, "E147.trimOffspring", {"start": v(-39.8, -28.06) * mm, "end": v(-34.47, -28.06) * mm});
            skLineSegment(sketch, "E148.trimOffspring", {"start": v(-39.8, -27.05) * mm, "end": v(-34.47, -27.05) * mm});
            skLineSegment(sketch, "E149.trimOffspring", {"start": v(-46.16, -27.05) * mm, "end": v(-40.82, -27.05) * mm});
            skLineSegment(sketch, "E150.trimOffspring", {"start": v(-46.16, -21.71) * mm, "end": v(-40.82, -21.71) * mm});
            skLineSegment(sketch, "E151.trimOffspring", {"start": v(-46.16, -20.7) * mm, "end": v(-40.82, -20.7) * mm});
            skLineSegment(sketch, "E152.trimOffspring", {"start": v(-46.16, -15.36) * mm, "end": v(-40.82, -15.36) * mm});
            skLineSegment(sketch, "E153.trimOffspring", {"start": v(-46.16, -14.35) * mm, "end": v(-40.82, -14.35) * mm});
            skLineSegment(sketch, "E154.trimOffspring", {"start": v(-52.5, -14.35) * mm, "end": v(-47.17, -14.35) * mm});
            skLineSegment(sketch, "E155.trimOffspring", {"start": v(-52.5, -15.36) * mm, "end": v(-47.17, -15.36) * mm});
            skLineSegment(sketch, "E156.trimOffspring", {"start": v(-52.5, -20.7) * mm, "end": v(-47.17, -20.7) * mm});
            skLineSegment(sketch, "E157.trimOffspring", {"start": v(-52.5, -21.71) * mm, "end": v(-47.17, -21.71) * mm});
            skLineSegment(sketch, "E158.trimOffspring", {"start": v(-52.5, -27.05) * mm, "end": v(-47.17, -27.05) * mm});
            skLineSegment(sketch, "E159.trimOffspring", {"start": v(-52.5, -28.06) * mm, "end": v(-47.17, -28.06) * mm});
            skLineSegment(sketch, "E160.trimOffspring", {"start": v(-58.86, -28.06) * mm, "end": v(-53.52, -28.06) * mm});
            skLineSegment(sketch, "E161.trimOffspring", {"start": v(-58.86, -27.05) * mm, "end": v(-53.52, -27.05) * mm});
            skLineSegment(sketch, "E162.trimOffspring", {"start": v(-58.86, -21.71) * mm, "end": v(-53.52, -21.71) * mm});
            skLineSegment(sketch, "E163.trimOffspring", {"start": v(-58.86, -20.7) * mm, "end": v(-53.52, -20.7) * mm});
            skLineSegment(sketch, "E164.trimOffspring", {"start": v(-58.86, -14.35) * mm, "end": v(-53.52, -14.35) * mm});
            skLineSegment(sketch, "E165.trimOffspring", {"start": v(-58.86, -15.36) * mm, "end": v(-53.52, -15.36) * mm});
            skLineSegment(sketch, "E166.trimOffspring", {"start": v(-65.2, -15.36) * mm, "end": v(-59.87, -15.36) * mm});
            skLineSegment(sketch, "E167.trimOffspring", {"start": v(-65.2, -14.35) * mm, "end": v(-59.87, -14.35) * mm});
            skLineSegment(sketch, "E168.trimOffspring", {"start": v(-65.2, -20.7) * mm, "end": v(-59.87, -20.7) * mm});
            skLineSegment(sketch, "E169.trimOffspring", {"start": v(-65.2, -21.71) * mm, "end": v(-59.87, -21.71) * mm});
            skLineSegment(sketch, "E170.trimOffspring", {"start": v(-65.2, -27.05) * mm, "end": v(-59.87, -27.05) * mm});
            skLineSegment(sketch, "E171.trimOffspring", {"start": v(-65.2, -28.06) * mm, "end": v(-59.87, -28.06) * mm});
            skLineSegment(sketch, "E172.trimOffspring", {"start": v(42.74, -9.01) * mm, "end": v(47.55, -9.01) * mm});
            skLineSegment(sketch, "E173.trimOffspring", {"start": v(42.74, -9.01) * mm, "end": v(47.3, -9.01) * mm});
            skLineSegment(sketch, "E174.trimOffspring", {"start": v(42.74, -8) * mm, "end": v(46.53, -8) * mm});
            skLineSegment(sketch, "E175.trimOffspring", {"start": v(42.74, -8) * mm, "end": v(46.78, -8) * mm});
            skLineSegment(sketch, "E176.trimOffspring", {"start": v(42.74, -8) * mm, "end": v(46.28, -8) * mm});
            skLineSegment(sketch, "E177.trimOffspring", {"start": v(42.74, -2.66) * mm, "end": v(47.55, -2.66) * mm});
            skLineSegment(sketch, "E178.trimOffspring", {"start": v(42.74, -2.66) * mm, "end": v(47.3, -2.66) * mm});
            skLineSegment(sketch, "E179.trimOffspring", {"start": v(42.74, -1.65) * mm, "end": v(46.78, -1.65) * mm});
            skLineSegment(sketch, "E180.trimOffspring", {"start": v(42.74, -1.65) * mm, "end": v(46.28, -1.65) * mm});
            skLineSegment(sketch, "E181.trimOffspring", {"start": v(42.74, -1.65) * mm, "end": v(46.53, -1.65) * mm});
            skLineSegment(sketch, "E182.trimOffspring", {"start": v(42.74, 3.69) * mm, "end": v(47.55, 3.69) * mm});
            skLineSegment(sketch, "E183.trimOffspring", {"start": v(42.74, 3.69) * mm, "end": v(47.3, 3.69) * mm});
            skLineSegment(sketch, "E184.trimOffspring", {"start": v(42.74, 4.7) * mm, "end": v(46.28, 4.7) * mm});
            skLineSegment(sketch, "E185.trimOffspring", {"start": v(42.74, 4.7) * mm, "end": v(46.53, 4.7) * mm});
            skLineSegment(sketch, "E186.trimOffspring", {"start": v(42.74, 4.7) * mm, "end": v(46.78, 4.7) * mm});
            skLineSegment(sketch, "E187.trimOffspring", {"start": v(42.74, 10.04) * mm, "end": v(47.3, 10.04) * mm});
            skLineSegment(sketch, "E188.trimOffspring", {"start": v(42.74, 10.04) * mm, "end": v(47.55, 10.04) * mm});
            skLineSegment(sketch, "E189.trimOffspring", {"start": v(42.74, 11.05) * mm, "end": v(46.28, 11.05) * mm});
            skLineSegment(sketch, "E190.trimOffspring", {"start": v(42.74, 11.05) * mm, "end": v(46.53, 11.05) * mm});
            skLineSegment(sketch, "E191.trimOffspring", {"start": v(42.74, 11.05) * mm, "end": v(46.78, 11.05) * mm});
            skLineSegment(sketch, "E192.trimOffspring", {"start": v(36.4, -9.01) * mm, "end": v(41.73, -9.01) * mm});
            skLineSegment(sketch, "E193.trimOffspring", {"start": v(36.4, -8) * mm, "end": v(41.73, -8) * mm});
            skLineSegment(sketch, "E194.trimOffspring", {"start": v(36.4, -2.66) * mm, "end": v(41.73, -2.66) * mm});
            skLineSegment(sketch, "E195.trimOffspring", {"start": v(36.4, -1.65) * mm, "end": v(41.73, -1.65) * mm});
            skLineSegment(sketch, "E196.trimOffspring", {"start": v(36.4, 3.69) * mm, "end": v(41.73, 3.69) * mm});
            skLineSegment(sketch, "E197.trimOffspring", {"start": v(36.4, 4.7) * mm, "end": v(41.73, 4.7) * mm});
            skLineSegment(sketch, "E198.trimOffspring", {"start": v(36.4, 10.04) * mm, "end": v(41.73, 10.04) * mm});
            skLineSegment(sketch, "E199.trimOffspring", {"start": v(36.4, 11.05) * mm, "end": v(41.73, 11.05) * mm});
            skLineSegment(sketch, "E200.trimOffspring", {"start": v(30.04, -9.01) * mm, "end": v(35.38, -9.01) * mm});
            skLineSegment(sketch, "E201.trimOffspring", {"start": v(30.04, -8) * mm, "end": v(35.38, -8) * mm});
            skLineSegment(sketch, "E202.trimOffspring", {"start": v(30.04, -2.66) * mm, "end": v(35.38, -2.66) * mm});
            skLineSegment(sketch, "E203.trimOffspring", {"start": v(30.04, -1.65) * mm, "end": v(35.38, -1.65) * mm});
            skLineSegment(sketch, "E204.trimOffspring", {"start": v(30.04, 3.69) * mm, "end": v(35.38, 3.69) * mm});
            skLineSegment(sketch, "E205.trimOffspring", {"start": v(30.04, 4.7) * mm, "end": v(35.38, 4.7) * mm});
            skLineSegment(sketch, "E206.trimOffspring", {"start": v(30.04, 11.05) * mm, "end": v(35.38, 11.05) * mm});
            skLineSegment(sketch, "E207.trimOffspring", {"start": v(30.04, 10.04) * mm, "end": v(35.38, 10.04) * mm});
            skLineSegment(sketch, "E208.trimOffspring", {"start": v(23.7, -9.01) * mm, "end": v(29.03, -9.01) * mm});
            skLineSegment(sketch, "E209.trimOffspring", {"start": v(23.7, -8) * mm, "end": v(29.03, -8) * mm});
            skLineSegment(sketch, "E210.trimOffspring", {"start": v(23.7, -2.66) * mm, "end": v(29.03, -2.66) * mm});
            skLineSegment(sketch, "E211.trimOffspring", {"start": v(23.7, -1.65) * mm, "end": v(29.03, -1.65) * mm});
            skLineSegment(sketch, "E212.trimOffspring", {"start": v(23.7, 3.69) * mm, "end": v(29.03, 3.69) * mm});
            skLineSegment(sketch, "E213.trimOffspring", {"start": v(23.7, 4.7) * mm, "end": v(29.03, 4.7) * mm});
            skLineSegment(sketch, "E214.trimOffspring", {"start": v(23.7, 10.04) * mm, "end": v(29.03, 10.04) * mm});
            skLineSegment(sketch, "E215.trimOffspring", {"start": v(23.7, 11.05) * mm, "end": v(29.03, 11.05) * mm});
            skLineSegment(sketch, "E216.trimOffspring", {"start": v(17.34, 11.05) * mm, "end": v(22.68, 11.05) * mm});
            skLineSegment(sketch, "E217.trimOffspring", {"start": v(17.34, 10.04) * mm, "end": v(22.68, 10.04) * mm});
            skLineSegment(sketch, "E218.trimOffspring", {"start": v(17.34, 4.7) * mm, "end": v(22.68, 4.7) * mm});
            skLineSegment(sketch, "E219.trimOffspring", {"start": v(17.34, 3.69) * mm, "end": v(22.68, 3.69) * mm});
            skLineSegment(sketch, "E220.trimOffspring", {"start": v(17.34, -1.65) * mm, "end": v(22.68, -1.65) * mm});
            skLineSegment(sketch, "E221.trimOffspring", {"start": v(17.34, -2.66) * mm, "end": v(22.68, -2.66) * mm});
            skLineSegment(sketch, "E222.trimOffspring", {"start": v(17.34, -8) * mm, "end": v(22.68, -8) * mm});
            skLineSegment(sketch, "E223.trimOffspring", {"start": v(17.34, -9.01) * mm, "end": v(22.68, -9.01) * mm});
            skLineSegment(sketch, "E224.trimOffspring", {"start": v(11, -9.01) * mm, "end": v(16.33, -9.01) * mm});
            skLineSegment(sketch, "E225.trimOffspring", {"start": v(11, -8) * mm, "end": v(16.33, -8) * mm});
            skLineSegment(sketch, "E226.trimOffspring", {"start": v(11, -2.66) * mm, "end": v(16.33, -2.66) * mm});
            skLineSegment(sketch, "E227.trimOffspring", {"start": v(11, -1.65) * mm, "end": v(16.33, -1.65) * mm});
            skLineSegment(sketch, "E228.trimOffspring", {"start": v(11, 3.69) * mm, "end": v(16.33, 3.69) * mm});
            skLineSegment(sketch, "E229.trimOffspring", {"start": v(11, 4.7) * mm, "end": v(16.33, 4.7) * mm});
            skLineSegment(sketch, "E230.trimOffspring", {"start": v(11, 10.04) * mm, "end": v(16.33, 10.04) * mm});
            skLineSegment(sketch, "E231.trimOffspring", {"start": v(11, 11.05) * mm, "end": v(16.33, 11.05) * mm});
            skLineSegment(sketch, "E232.trimOffspring", {"start": v(4.64, -9.01) * mm, "end": v(9.98, -9.01) * mm});
            skLineSegment(sketch, "E233.trimOffspring", {"start": v(4.64, -8) * mm, "end": v(9.98, -8) * mm});
            skLineSegment(sketch, "E234.trimOffspring", {"start": v(4.64, -2.66) * mm, "end": v(9.98, -2.66) * mm});
            skLineSegment(sketch, "E235.trimOffspring", {"start": v(4.64, -1.65) * mm, "end": v(9.98, -1.65) * mm});
            skLineSegment(sketch, "E236.trimOffspring", {"start": v(4.64, 3.69) * mm, "end": v(9.98, 3.69) * mm});
            skLineSegment(sketch, "E237.trimOffspring", {"start": v(4.64, 4.7) * mm, "end": v(9.98, 4.7) * mm});
            skLineSegment(sketch, "E238.trimOffspring", {"start": v(4.64, 10.04) * mm, "end": v(9.98, 10.04) * mm});
            skLineSegment(sketch, "E239.trimOffspring", {"start": v(4.64, 11.05) * mm, "end": v(9.98, 11.05) * mm});
            skLineSegment(sketch, "E240.trimOffspring", {"start": v(-1.7, -2.66) * mm, "end": v(3.63, -2.66) * mm});
            skLineSegment(sketch, "E241.trimOffspring", {"start": v(-1.7, -1.65) * mm, "end": v(3.63, -1.65) * mm});
            skLineSegment(sketch, "E242.trimOffspring", {"start": v(-1.7, 3.69) * mm, "end": v(3.63, 3.69) * mm});
            skLineSegment(sketch, "E243.trimOffspring", {"start": v(-1.7, 4.7) * mm, "end": v(3.63, 4.7) * mm});
            skLineSegment(sketch, "E244.trimOffspring", {"start": v(-1.7, 10.04) * mm, "end": v(3.63, 10.04) * mm});
            skLineSegment(sketch, "E245.trimOffspring", {"start": v(-1.7, 11.05) * mm, "end": v(3.63, 11.05) * mm});
            skLineSegment(sketch, "E246.trimOffspring", {"start": v(-8.06, -9.01) * mm, "end": v(-2.72, -9.01) * mm});
            skLineSegment(sketch, "E247.trimOffspring", {"start": v(-8.06, -8) * mm, "end": v(-2.72, -8) * mm});
            skLineSegment(sketch, "E248.trimOffspring", {"start": v(-8.06, -2.66) * mm, "end": v(-2.72, -2.66) * mm});
            skLineSegment(sketch, "E249.trimOffspring", {"start": v(-14.4, -9.01) * mm, "end": v(-9.07, -9.01) * mm});
            skLineSegment(sketch, "E250.trimOffspring", {"start": v(-14.4, -8) * mm, "end": v(-9.07, -8) * mm});
            skLineSegment(sketch, "E251.trimOffspring", {"start": v(-14.4, -2.66) * mm, "end": v(-9.07, -2.66) * mm});
            skLineSegment(sketch, "E252.trimOffspring", {"start": v(-14.4, -1.65) * mm, "end": v(-9.07, -1.65) * mm});
            skLineSegment(sketch, "E253.trimOffspring", {"start": v(-14.4, 3.69) * mm, "end": v(-9.07, 3.69) * mm});
            skLineSegment(sketch, "E254.trimOffspring", {"start": v(-14.4, 4.7) * mm, "end": v(-9.07, 4.7) * mm});
            skLineSegment(sketch, "E255.trimOffspring", {"start": v(-8.06, -1.65) * mm, "end": v(-2.72, -1.65) * mm});
            skLineSegment(sketch, "E256.trimOffspring", {"start": v(-20.76, -9.01) * mm, "end": v(-15.42, -9.01) * mm});
            skLineSegment(sketch, "E257.trimOffspring", {"start": v(-27.1, -9.01) * mm, "end": v(-21.77, -9.01) * mm});
            skLineSegment(sketch, "E258.trimOffspring", {"start": v(-27.1, -8) * mm, "end": v(-21.77, -8) * mm});
            skLineSegment(sketch, "E259.trimOffspring", {"start": v(-20.76, -8) * mm, "end": v(-15.42, -8) * mm});
            skLineSegment(sketch, "E260.trimOffspring", {"start": v(-20.76, -2.66) * mm, "end": v(-15.42, -2.66) * mm});
            skLineSegment(sketch, "E261.trimOffspring", {"start": v(-20.76, -1.65) * mm, "end": v(-15.42, -1.65) * mm});
            skLineSegment(sketch, "E262.trimOffspring", {"start": v(-27.1, -2.66) * mm, "end": v(-21.77, -2.66) * mm});
            skLineSegment(sketch, "E263.trimOffspring", {"start": v(-27.1, -1.65) * mm, "end": v(-21.77, -1.65) * mm});
            skLineSegment(sketch, "E264.trimOffspring", {"start": v(-8.06, 3.69) * mm, "end": v(-2.72, 3.69) * mm});
            skLineSegment(sketch, "E265.trimOffspring", {"start": v(-8.06, 3.69) * mm, "end": v(-8.06, -1.65) * mm});
            skLineSegment(sketch, "E266.trimOffspring", {"start": v(-8.06, 4.7) * mm, "end": v(-2.72, 4.7) * mm});
            skLineSegment(sketch, "E267.trimOffspring", {"start": v(-20.76, 3.69) * mm, "end": v(-15.42, 3.69) * mm});
            skLineSegment(sketch, "E268.trimOffspring", {"start": v(-20.76, 4.7) * mm, "end": v(-15.42, 4.7) * mm});
            skLineSegment(sketch, "E269.trimOffspring", {"start": v(-27.1, 3.69) * mm, "end": v(-21.77, 3.69) * mm});
            skLineSegment(sketch, "E270.trimOffspring", {"start": v(-27.1, 4.7) * mm, "end": v(-21.77, 4.7) * mm});
            skLineSegment(sketch, "E271.trimOffspring", {"start": v(-33.46, -9.01) * mm, "end": v(-28.12, -9.01) * mm});
            skLineSegment(sketch, "E272.trimOffspring", {"start": v(-33.46, -8) * mm, "end": v(-28.12, -8) * mm});
            skLineSegment(sketch, "E273.trimOffspring", {"start": v(-8.06, 10.04) * mm, "end": v(-2.72, 10.04) * mm});
            skLineSegment(sketch, "E274.trimOffspring", {"start": v(-8.06, 11.05) * mm, "end": v(-2.72, 11.05) * mm});
            skLineSegment(sketch, "E275.trimOffspring", {"start": v(-14.4, 10.04) * mm, "end": v(-9.07, 10.04) * mm});
            skLineSegment(sketch, "E276.trimOffspring", {"start": v(-14.4, 11.05) * mm, "end": v(-9.07, 11.05) * mm});
            skLineSegment(sketch, "E277.trimOffspring", {"start": v(-20.76, 10.04) * mm, "end": v(-15.42, 10.04) * mm});
            skLineSegment(sketch, "E278.trimOffspring", {"start": v(-20.76, 11.05) * mm, "end": v(-15.42, 11.05) * mm});
            skLineSegment(sketch, "E279.trimOffspring", {"start": v(-27.1, 10.04) * mm, "end": v(-21.77, 10.04) * mm});
            skLineSegment(sketch, "E280.trimOffspring", {"start": v(-27.1, 11.05) * mm, "end": v(-21.77, 11.05) * mm});
            skLineSegment(sketch, "E281.trimOffspring", {"start": v(-33.46, -2.66) * mm, "end": v(-28.12, -2.66) * mm});
            skLineSegment(sketch, "E282.trimOffspring", {"start": v(-33.46, -1.65) * mm, "end": v(-28.12, -1.65) * mm});
            skLineSegment(sketch, "E283.trimOffspring", {"start": v(-33.46, 3.69) * mm, "end": v(-28.12, 3.69) * mm});
            skLineSegment(sketch, "E284.trimOffspring", {"start": v(-33.46, 4.7) * mm, "end": v(-28.12, 4.7) * mm});
            skLineSegment(sketch, "E285.trimOffspring", {"start": v(-33.46, 10.04) * mm, "end": v(-28.12, 10.04) * mm});
            skLineSegment(sketch, "E286.trimOffspring", {"start": v(-33.46, 11.05) * mm, "end": v(-28.12, 11.05) * mm});
            skLineSegment(sketch, "E287.trimOffspring", {"start": v(-39.8, 11.05) * mm, "end": v(-34.47, 11.05) * mm});
            skLineSegment(sketch, "E288.trimOffspring", {"start": v(-39.8, 10.04) * mm, "end": v(-34.47, 10.04) * mm});
            skLineSegment(sketch, "E289.trimOffspring", {"start": v(-39.8, 4.7) * mm, "end": v(-34.47, 4.7) * mm});
            skLineSegment(sketch, "E290.trimOffspring", {"start": v(-39.8, 3.69) * mm, "end": v(-34.47, 3.69) * mm});
            skLineSegment(sketch, "E291.trimOffspring", {"start": v(-39.8, -1.65) * mm, "end": v(-34.47, -1.65) * mm});
            skLineSegment(sketch, "E292.trimOffspring", {"start": v(-39.8, -2.66) * mm, "end": v(-34.47, -2.66) * mm});
            skLineSegment(sketch, "E293.trimOffspring", {"start": v(-39.8, -8) * mm, "end": v(-34.47, -8) * mm});
            skLineSegment(sketch, "E294.trimOffspring", {"start": v(-39.8, -9.01) * mm, "end": v(-34.47, -9.01) * mm});
            skLineSegment(sketch, "E295.trimOffspring", {"start": v(-39.8, -15.36) * mm, "end": v(-39.8, -20.7) * mm});
            skLineSegment(sketch, "E296.trimOffspring", {"start": v(-46.16, -9.01) * mm, "end": v(-40.82, -9.01) * mm});
            skLineSegment(sketch, "E297.trimOffspring", {"start": v(-46.16, -8) * mm, "end": v(-40.82, -8) * mm});
            skLineSegment(sketch, "E298.trimOffspring", {"start": v(-46.16, -2.66) * mm, "end": v(-40.82, -2.66) * mm});
            skLineSegment(sketch, "E299.trimOffspring", {"start": v(-46.16, -1.65) * mm, "end": v(-40.82, -1.65) * mm});
            skLineSegment(sketch, "E300.trimOffspring", {"start": v(-46.16, 3.69) * mm, "end": v(-40.82, 3.69) * mm});
            skLineSegment(sketch, "E301.trimOffspring", {"start": v(-46.16, 4.7) * mm, "end": v(-40.82, 4.7) * mm});
            skLineSegment(sketch, "E302.trimOffspring", {"start": v(-46.16, 10.04) * mm, "end": v(-40.82, 10.04) * mm});
            skLineSegment(sketch, "E303.trimOffspring", {"start": v(-46.16, 10.04) * mm, "end": v(-46.16, 4.7) * mm});
            skLineSegment(sketch, "E304.trimOffspring", {"start": v(-46.16, 11.05) * mm, "end": v(-40.82, 11.05) * mm});
            skLineSegment(sketch, "E305.trimOffspring", {"start": v(-52.5, -9.01) * mm, "end": v(-47.17, -9.01) * mm});
            skLineSegment(sketch, "E306.trimOffspring", {"start": v(-52.5, 11.05) * mm, "end": v(-47.17, 11.05) * mm});
            skLineSegment(sketch, "E307.trimOffspring", {"start": v(-52.5, 10.04) * mm, "end": v(-47.17, 10.04) * mm});
            skLineSegment(sketch, "E308.trimOffspring", {"start": v(-52.5, 4.7) * mm, "end": v(-47.17, 4.7) * mm});
            skLineSegment(sketch, "E309.trimOffspring", {"start": v(-52.5, 3.69) * mm, "end": v(-47.17, 3.69) * mm});
            skLineSegment(sketch, "E310.trimOffspring", {"start": v(-53.52, 3.69) * mm, "end": v(-53.52, -34.16) * mm});
            skLineSegment(sketch, "E311.trimOffspring", {"start": v(-58.86, 3.69) * mm, "end": v(-58.86, -1.65) * mm});
            skLineSegment(sketch, "E312.trimOffspring", {"start": v(-52.5, -1.65) * mm, "end": v(-47.17, -1.65) * mm});
            skLineSegment(sketch, "E313.trimOffspring", {"start": v(-52.5, -2.66) * mm, "end": v(-47.17, -2.66) * mm});
            skLineSegment(sketch, "E314.trimOffspring", {"start": v(-52.5, -8) * mm, "end": v(-47.17, -8) * mm});
            skLineSegment(sketch, "E315.trimOffspring", {"start": v(-58.86, 11.05) * mm, "end": v(-53.52, 11.05) * mm});
            skLineSegment(sketch, "E316.trimOffspring", {"start": v(-58.86, 10.04) * mm, "end": v(-53.52, 10.04) * mm});
            skLineSegment(sketch, "E317.trimOffspring", {"start": v(-58.86, 4.7) * mm, "end": v(-53.52, 4.7) * mm});
            skLineSegment(sketch, "E318.trimOffspring", {"start": v(-58.86, 3.69) * mm, "end": v(-53.52, 3.69) * mm});
            skLineSegment(sketch, "E319.trimOffspring", {"start": v(-58.86, -1.65) * mm, "end": v(-53.52, -1.65) * mm});
            skLineSegment(sketch, "E320.trimOffspring", {"start": v(-58.86, -2.66) * mm, "end": v(-53.52, -2.66) * mm});
            skLineSegment(sketch, "E321.trimOffspring", {"start": v(-58.86, -8) * mm, "end": v(-53.52, -8) * mm});
            skLineSegment(sketch, "E322.trimOffspring", {"start": v(-58.86, -9.01) * mm, "end": v(-53.52, -9.01) * mm});
            skLineSegment(sketch, "E323.trimOffspring", {"start": v(-65.2, 11.05) * mm, "end": v(-59.87, 11.05) * mm});
            skLineSegment(sketch, "E324.trimOffspring", {"start": v(-65.2, 10.04) * mm, "end": v(-59.87, 10.04) * mm});
            skLineSegment(sketch, "E325.trimOffspring", {"start": v(-65.2, 4.7) * mm, "end": v(-59.87, 4.7) * mm});
            skLineSegment(sketch, "E326.trimOffspring", {"start": v(-65.2, 3.69) * mm, "end": v(-59.87, 3.69) * mm});
            skLineSegment(sketch, "E327.trimOffspring", {"start": v(-65.2, -1.65) * mm, "end": v(-59.87, -1.65) * mm});
            skLineSegment(sketch, "E328.trimOffspring", {"start": v(-65.2, -2.66) * mm, "end": v(-59.87, -2.66) * mm});
            skLineSegment(sketch, "E329.trimOffspring", {"start": v(-65.2, -8) * mm, "end": v(-59.87, -8) * mm});
            skLineSegment(sketch, "E330.trimOffspring", {"start": v(-65.2, -9.01) * mm, "end": v(-59.87, -9.01) * mm});
            skLineSegment(sketch, "E331.trimOffspring", {"start": v(-8.06, 21) * mm, "end": v(-2.72, 21) * mm});
            skLineSegment(sketch, "E332.trimOffspring", {"start": v(-9.07, 16.39) * mm, "end": v(-9.07, 4.7) * mm});
            skLineSegment(sketch, "E333.trimOffspring", {"start": v(-8.06, 16.39) * mm, "end": v(-8.06, 11.05) * mm});
            skLineSegment(sketch, "E334.trimOffspring", {"start": v(-14.4, 16.39) * mm, "end": v(-14.4, 11.05) * mm});
            skLineSegment(sketch, "E335.trimOffspring", {"start": v(-14.4, 17.4) * mm, "end": v(-9.07, 17.4) * mm});
            skLineSegment(sketch, "E336.trimOffspring", {"start": v(-15.42, 16.39) * mm, "end": v(-15.42, 4.7) * mm});
            skLineSegment(sketch, "E337.trimOffspring", {"start": v(-14.4, 16.39) * mm, "end": v(-9.07, 16.39) * mm});
            skLineSegment(sketch, "E338.trimOffspring", {"start": v(-8.06, 17.4) * mm, "end": v(-2.72, 17.4) * mm});
            skLineSegment(sketch, "E339.trimOffspring", {"start": v(42.74, 17.4) * mm, "end": v(46.53, 17.4) * mm});
            skLineSegment(sketch, "E340.trimOffspring", {"start": v(42.74, 17.4) * mm, "end": v(46.78, 17.4) * mm});
            skLineSegment(sketch, "E341.trimOffspring", {"start": v(42.74, 17.4) * mm, "end": v(46.28, 17.4) * mm});
            skLineSegment(sketch, "E342.trimOffspring", {"start": v(42.74, 16.39) * mm, "end": v(47.55, 16.39) * mm});
            skLineSegment(sketch, "E343.trimOffspring", {"start": v(42.74, 16.39) * mm, "end": v(47.8, 16.39) * mm});
            skLineSegment(sketch, "E344.trimOffspring", {"start": v(42.74, 16.39) * mm, "end": v(47.3, 16.39) * mm});
            skLineSegment(sketch, "E345.trimOffspring", {"start": v(36.4, 17.4) * mm, "end": v(41.73, 17.4) * mm});
            skLineSegment(sketch, "E346.trimOffspring", {"start": v(36.4, 16.39) * mm, "end": v(41.73, 16.39) * mm});
            skLineSegment(sketch, "E347.trimOffspring", {"start": v(30.04, 17.4) * mm, "end": v(35.38, 17.4) * mm});
            skLineSegment(sketch, "E348.trimOffspring", {"start": v(30.04, 16.39) * mm, "end": v(35.38, 16.39) * mm});
            skLineSegment(sketch, "E349.trimOffspring", {"start": v(23.7, 17.4) * mm, "end": v(29.03, 17.4) * mm});
            skLineSegment(sketch, "E350.trimOffspring", {"start": v(23.7, 16.39) * mm, "end": v(29.03, 16.39) * mm});
            skLineSegment(sketch, "E351.trimOffspring", {"start": v(17.34, 17.4) * mm, "end": v(22.68, 17.4) * mm});
            skLineSegment(sketch, "E352.trimOffspring", {"start": v(17.34, 16.39) * mm, "end": v(22.68, 16.39) * mm});
            skLineSegment(sketch, "E353.trimOffspring", {"start": v(11, 17.4) * mm, "end": v(16.33, 17.4) * mm});
            skLineSegment(sketch, "E354.trimOffspring", {"start": v(11, 16.39) * mm, "end": v(16.33, 16.39) * mm});
            skLineSegment(sketch, "E355.trimOffspring", {"start": v(4.64, 17.4) * mm, "end": v(9.98, 17.4) * mm});
            skLineSegment(sketch, "E356.trimOffspring", {"start": v(4.64, 16.39) * mm, "end": v(9.98, 16.39) * mm});
            skLineSegment(sketch, "E357.trimOffspring", {"start": v(-1.7, 17.4) * mm, "end": v(3.63, 17.4) * mm});
            skLineSegment(sketch, "E358.trimOffspring", {"start": v(-1.7, 16.39) * mm, "end": v(3.63, 16.39) * mm});
            skLineSegment(sketch, "E359.trimOffspring", {"start": v(-8.06, 16.39) * mm, "end": v(-2.72, 16.39) * mm});
            skLineSegment(sketch, "E360.trimOffspring", {"start": v(-20.76, 17.4) * mm, "end": v(-15.42, 17.4) * mm});
            skLineSegment(sketch, "E361.trimOffspring", {"start": v(-20.76, 16.39) * mm, "end": v(-15.42, 16.39) * mm});
            skLineSegment(sketch, "E362.trimOffspring", {"start": v(-27.1, 17.4) * mm, "end": v(-21.77, 17.4) * mm});
            skLineSegment(sketch, "E363.trimOffspring", {"start": v(-27.1, 16.39) * mm, "end": v(-21.77, 16.39) * mm});
            skLineSegment(sketch, "E364.trimOffspring", {"start": v(-33.46, 17.4) * mm, "end": v(-28.12, 17.4) * mm});
            skLineSegment(sketch, "E365.trimOffspring", {"start": v(-33.46, 16.39) * mm, "end": v(-28.12, 16.39) * mm});
            skLineSegment(sketch, "E366.trimOffspring", {"start": v(-39.8, 17.4) * mm, "end": v(-34.47, 17.4) * mm});
            skLineSegment(sketch, "E367.trimOffspring", {"start": v(-39.8, 16.39) * mm, "end": v(-34.47, 16.39) * mm});
            skLineSegment(sketch, "E368.trimOffspring", {"start": v(-46.16, 17.4) * mm, "end": v(-40.82, 17.4) * mm});
            skLineSegment(sketch, "E369.trimOffspring", {"start": v(-46.16, 16.39) * mm, "end": v(-40.82, 16.39) * mm});
            skLineSegment(sketch, "E370.trimOffspring", {"start": v(-52.5, 17.4) * mm, "end": v(-47.17, 17.4) * mm});
            skLineSegment(sketch, "E371.trimOffspring", {"start": v(-52.5, 16.39) * mm, "end": v(-47.17, 16.39) * mm});
            skLineSegment(sketch, "E372.trimOffspring", {"start": v(-58.86, 17.4) * mm, "end": v(-53.52, 17.4) * mm});
            skLineSegment(sketch, "E373.trimOffspring", {"start": v(-58.86, 16.39) * mm, "end": v(-53.52, 16.39) * mm});
            skLineSegment(sketch, "E374.trimOffspring", {"start": v(-65.2, 17.4) * mm, "end": v(-59.87, 17.4) * mm});
            skLineSegment(sketch, "E375.trimOffspring", {"start": v(-65.2, 16.39) * mm, "end": v(-59.87, 16.39) * mm});
            skLineSegment(sketch, "E376.trimOffspring", {"start": v(-27.1, 21) * mm, "end": v(-21.77, 21) * mm});
            skLineSegment(sketch, "E377.trimOffspring", {"start": v(-20.76, 21) * mm, "end": v(-15.42, 21) * mm});
            skLineSegment(sketch, "E378", {"start": v(-33.46, 21) * mm, "end": v(-28.12, 21) * mm});
            skLineSegment(sketch, "E379.trimOffspring", {"start": v(-40.82, 16.39) * mm, "end": v(-40.82, 10.04) * mm});
            skLineSegment(sketch, "E380.trimOffspring", {"start": v(-39.8, 16.39) * mm, "end": v(-39.8, 11.05) * mm});
            skLineSegment(sketch, "E381.trimOffspring", {"start": v(42.74, 21) * mm, "end": v(46.78, 21) * mm});
            skLineSegment(sketch, "E382.trimOffspring", {"start": v(36.4, 21) * mm, "end": v(41.73, 21) * mm});
            skLineSegment(sketch, "E383.trimOffspring", {"start": v(30.04, 21) * mm, "end": v(35.38, 21) * mm});
            skLineSegment(sketch, "E384.trimOffspring", {"start": v(23.7, 21) * mm, "end": v(29.03, 21) * mm});
            skLineSegment(sketch, "E385.trimOffspring", {"start": v(17.34, 21) * mm, "end": v(22.68, 21) * mm});
            skLineSegment(sketch, "E386.trimOffspring", {"start": v(11, 21) * mm, "end": v(16.33, 21) * mm});
            skLineSegment(sketch, "E387.trimOffspring", {"start": v(4.64, 21) * mm, "end": v(9.98, 21) * mm});
            skLineSegment(sketch, "E388.trimOffspring", {"start": v(-1.7, 21) * mm, "end": v(3.63, 21) * mm});
            skLineSegment(sketch, "E389.trimOffspring", {"start": v(-58.86, 21) * mm, "end": v(-53.52, 21) * mm});
            skLineSegment(sketch, "E390.trimOffspring", {"start": v(-46.16, 21) * mm, "end": v(-40.82, 21) * mm});
            skLineSegment(sketch, "E391.trimOffspring", {"start": v(-52.5, 21) * mm, "end": v(-47.17, 21) * mm});
            skLineSegment(sketch, "E392.trimOffspring", {"start": v(-65.2, 21) * mm, "end": v(-59.87, 21) * mm});
            skLineSegment(sketch, "E393.trimOffspring", {"start": v(-34.47, 3.69) * mm, "end": v(-34.47, -27.05) * mm});
            skLineSegment(sketch, "E394.trimOffspring", {"start": v(-33.46, 3.69) * mm, "end": v(-33.46, -1.65) * mm});
            skLineSegment(sketch, "E395.trimOffspring", {"start": v(-34.47, 3.69) * mm, "end": v(-34.47, -34.16) * mm});
            skLineSegment(sketch, "E396.trimOffspring", {"start": v(-28.12, -9.01) * mm, "end": v(-28.12, -34.16) * mm});
            skLineSegment(sketch, "E397.trimOffspring", {"start": v(-21.77, -15.36) * mm, "end": v(-21.77, -20.7) * mm});
            skLineSegment(sketch, "E398.trimOffspring", {"start": v(-20.76, -9.01) * mm, "end": v(-20.76, -14.35) * mm});
            skLineSegment(sketch, "E399.trimOffspring", {"start": v(-21.77, -9.01) * mm, "end": v(-21.77, -14.35) * mm});
            skLineSegment(sketch, "E400.trimOffspring", {"start": v(4.64, 3.69) * mm, "end": v(4.64, -1.65) * mm});
            skLineSegment(sketch, "E401.trimOffspring", {"start": v(3.63, 3.69) * mm, "end": v(3.63, -34.16) * mm});
            skLineSegment(sketch, "E402.trimOffspring", {"start": v(9.98, 3.69) * mm, "end": v(9.98, -14.35) * mm});
            skLineSegment(sketch, "E403.trimOffspring", {"start": v(-1.7, -2.66) * mm, "end": v(-1.7, -8) * mm});
            skLineSegment(sketch, "E404.trimOffspring", {"start": v(-8.06, -2.66) * mm, "end": v(-8.06, -8) * mm});
            skLineSegment(sketch, "E405.trimOffspring", {"start": v(-9.07, -2.66) * mm, "end": v(-9.07, -9.01) * mm});
            skLineSegment(sketch, "E406.trimOffspring", {"start": v(-14.4, -2.66) * mm, "end": v(-14.4, -8) * mm});
            skLineSegment(sketch, "E407.trimOffspring", {"start": v(-15.42, -2.66) * mm, "end": v(-15.42, -14.35) * mm});
            skLineSegment(sketch, "E408.trimOffspring", {"start": v(-20.76, -2.66) * mm, "end": v(-20.76, -8) * mm});
            skLineSegment(sketch, "E409.trimOffspring", {"start": v(-20.76, 3.69) * mm, "end": v(-20.76, -1.65) * mm});
            skLineSegment(sketch, "E410.trimOffspring", {"start": v(-14.4, 3.69) * mm, "end": v(-14.4, -1.65) * mm});
            skLineSegment(sketch, "E411.trimOffspring", {"start": v(-1.7, 3.69) * mm, "end": v(-1.7, -1.65) * mm});
            skLineSegment(sketch, "E412.trimOffspring", {"start": v(17.34, 3.69) * mm, "end": v(17.34, -1.65) * mm});
            skLineSegment(sketch, "E413.trimOffspring", {"start": v(23.7, 3.69) * mm, "end": v(23.7, -1.65) * mm});
            skLineSegment(sketch, "E414.trimOffspring", {"start": v(23.7, 10.04) * mm, "end": v(23.7, 4.7) * mm});
            skLineSegment(sketch, "E415.trimOffspring", {"start": v(17.34, 10.04) * mm, "end": v(17.34, 4.7) * mm});
            skLineSegment(sketch, "E416.trimOffspring", {"start": v(11, 10.04) * mm, "end": v(11, 4.7) * mm});
            skLineSegment(sketch, "E417.trimOffspring", {"start": v(4.64, 10.04) * mm, "end": v(4.64, 4.7) * mm});
            skLineSegment(sketch, "E418.trimOffspring", {"start": v(-1.7, 10.04) * mm, "end": v(-1.7, 4.7) * mm});
            skLineSegment(sketch, "E419.trimOffspring", {"start": v(30.04, 10.04) * mm, "end": v(30.04, 4.7) * mm});
            skLineSegment(sketch, "E420.trimOffspring", {"start": v(36.4, 10.04) * mm, "end": v(36.4, 4.7) * mm});
            skLineSegment(sketch, "E421.trimOffspring", {"start": v(42.74, 10.04) * mm, "end": v(42.74, 4.7) * mm});
            skLineSegment(sketch, "E422.trimOffspring", {"start": v(30.04, 3.69) * mm, "end": v(30.04, -1.65) * mm});
            skLineSegment(sketch, "E423.trimOffspring", {"start": v(17.34, 16.39) * mm, "end": v(17.34, 11.05) * mm});
            skLineSegment(sketch, "E424.trimOffspring", {"start": v(23.7, 16.39) * mm, "end": v(23.7, 11.05) * mm});
            skLineSegment(sketch, "E425.trimOffspring", {"start": v(11, 16.39) * mm, "end": v(11, 11.05) * mm});
            skLineSegment(sketch, "E426.trimOffspring", {"start": v(4.64, 16.39) * mm, "end": v(4.64, 11.05) * mm});
            skLineSegment(sketch, "E427.trimOffspring", {"start": v(-1.7, 16.39) * mm, "end": v(-1.7, 11.05) * mm});
            skLineSegment(sketch, "E428.trimOffspring", {"start": v(30.04, 16.39) * mm, "end": v(30.04, 11.05) * mm});
            skLineSegment(sketch, "E429.trimOffspring", {"start": v(36.4, 16.39) * mm, "end": v(36.4, 11.05) * mm});
            skPoint(sketch, "E430.orphan", {"position": v(17.34, 22.01) * mm});
            skLineSegment(sketch, "E431.trimOffspring", {"start": v(36.4, 3.69) * mm, "end": v(36.4, -1.65) * mm});
            skLineSegment(sketch, "E432.trimOffspring", {"start": v(23.7, -2.66) * mm, "end": v(23.7, -8) * mm});
            skLineSegment(sketch, "E433.trimOffspring", {"start": v(4.64, -2.66) * mm, "end": v(4.64, -8) * mm});
            skPoint(sketch, "E434.orphan", {"position": v(42.74, 22.01) * mm});
            skLineSegment(sketch, "E435.trimOffspring", {"start": v(11, -2.66) * mm, "end": v(11, -8) * mm});
            skLineSegment(sketch, "E436.trimOffspring", {"start": v(30.04, -2.66) * mm, "end": v(30.04, -8) * mm});
            skLineSegment(sketch, "E437.trimOffspring", {"start": v(36.4, 3.69) * mm, "end": v(36.4, -2.66) * mm});
            skLineSegment(sketch, "E438.trimOffspring", {"start": v(42.74, 3.69) * mm, "end": v(42.74, -1.65) * mm});
            skLineSegment(sketch, "E439.trimOffspring", {"start": v(4.64, -9.01) * mm, "end": v(4.64, -14.35) * mm});
            skLineSegment(sketch, "E440.trimOffspring", {"start": v(17.34, -9.01) * mm, "end": v(17.34, -14.35) * mm});
            skLineSegment(sketch, "E441", {"start": v(11, -1.65) * mm, "end": v(11, 3.69) * mm});
            skLineSegment(sketch, "E442.trimOffspring", {"start": v(42.74, -2.66) * mm, "end": v(42.74, -8) * mm});
            skLineSegment(sketch, "E443.trimOffspring", {"start": v(36.4, -9.01) * mm, "end": v(36.4, -14.35) * mm});
            skLineSegment(sketch, "E444.trimOffspring", {"start": v(42.74, -15.36) * mm, "end": v(42.74, -27.05) * mm});
            skLineSegment(sketch, "E445.trimOffspring", {"start": v(30.04, -15.36) * mm, "end": v(30.04, -20.7) * mm});
            skLineSegment(sketch, "E446.trimOffspring", {"start": v(30.04, -9.01) * mm, "end": v(30.04, -14.35) * mm});
            skLineSegment(sketch, "E447.trimOffspring", {"start": v(4.64, -15.36) * mm, "end": v(4.64, -20.7) * mm});
            skLineSegment(sketch, "E448.trimOffspring", {"start": v(-8.06, -9.01) * mm, "end": v(-8.06, -14.35) * mm});
            skLineSegment(sketch, "E449.trimOffspring", {"start": v(11, -9.01) * mm, "end": v(11, -14.35) * mm});
            skLineSegment(sketch, "E450", {"start": v(17.34, -8) * mm, "end": v(17.34, -2.66) * mm});
            skLineSegment(sketch, "E451.trimOffspring", {"start": v(11, -21.71) * mm, "end": v(11, -27.05) * mm});
            skLineSegment(sketch, "E452.trimOffspring", {"start": v(4.64, -21.71) * mm, "end": v(4.64, -27.05) * mm});
            skLineSegment(sketch, "E453.trimOffspring", {"start": v(-1.7, -21.71) * mm, "end": v(-1.7, -27.05) * mm});
            skLineSegment(sketch, "E454.trimOffspring", {"start": v(-8.06, -21.71) * mm, "end": v(-8.06, -27.05) * mm});
            skLineSegment(sketch, "E455.trimOffspring", {"start": v(-14.4, -21.71) * mm, "end": v(-14.4, -27.05) * mm});
            skLineSegment(sketch, "E456.trimOffspring", {"start": v(-14.4, -15.36) * mm, "end": v(-14.4, -20.7) * mm});
            skLineSegment(sketch, "E457.trimOffspring", {"start": v(-8.06, -15.36) * mm, "end": v(-8.06, -20.7) * mm});
            skLineSegment(sketch, "E458.trimOffspring", {"start": v(-14.4, -9.01) * mm, "end": v(-14.4, -14.35) * mm});
            skLineSegment(sketch, "E459.trimOffspring", {"start": v(16.33, 3.69) * mm, "end": v(16.33, -14.35) * mm});
            skLineSegment(sketch, "E460.trimOffspring", {"start": v(22.68, 3.69) * mm, "end": v(22.68, -34.16) * mm});
            skLineSegment(sketch, "E461.trimOffspring", {"start": v(29.03, 3.69) * mm, "end": v(29.03, -34.16) * mm});
            skLineSegment(sketch, "E462.trimOffspring", {"start": v(-2.72, 3.69) * mm, "end": v(-2.72, -8) * mm});
            skLineSegment(sketch, "E463.trimOffspring", {"start": v(-9.07, 3.69) * mm, "end": v(-9.07, -1.65) * mm});
            skLineSegment(sketch, "E464.trimOffspring", {"start": v(-15.42, 3.69) * mm, "end": v(-15.42, -1.65) * mm});
            skLineSegment(sketch, "E465.trimOffspring", {"start": v(22.68, 10.04) * mm, "end": v(22.68, 4.7) * mm});
            skLineSegment(sketch, "E466.trimOffspring", {"start": v(16.33, 10.04) * mm, "end": v(16.33, 4.7) * mm});
            skLineSegment(sketch, "E467.trimOffspring", {"start": v(16.33, 10.04) * mm, "end": v(16.33, -34.16) * mm});
            skLineSegment(sketch, "E468.trimOffspring", {"start": v(9.98, 3.69) * mm, "end": v(9.98, -34.16) * mm});
            skLineSegment(sketch, "E469.trimOffspring", {"start": v(-2.72, 3.69) * mm, "end": v(-2.72, -34.16) * mm});
            skLineSegment(sketch, "E470.trimOffspring", {"start": v(-15.42, 3.69) * mm, "end": v(-15.42, -34.16) * mm});
            skLineSegment(sketch, "E471.trimOffspring", {"start": v(22.68, 10.04) * mm, "end": v(22.68, -34.16) * mm});
            skLineSegment(sketch, "E472.trimOffspring", {"start": v(29.03, 10.04) * mm, "end": v(29.03, 4.7) * mm});
            skLineSegment(sketch, "E473.trimOffspring", {"start": v(9.98, 10.04) * mm, "end": v(9.98, 4.7) * mm});
            skLineSegment(sketch, "E474.trimOffspring", {"start": v(29.03, 10.04) * mm, "end": v(29.03, -34.41) * mm});
            skLineSegment(sketch, "E475.trimOffspring", {"start": v(23.7, -28.06) * mm, "end": v(23.7, -33.4) * mm});
            skLineSegment(sketch, "E476.trimOffspring", {"start": v(30.04, -28.06) * mm, "end": v(30.04, -33.4) * mm});
            skLineSegment(sketch, "E477.trimOffspring", {"start": v(36.4, -28.06) * mm, "end": v(36.4, -33.4) * mm});
            skLineSegment(sketch, "E478.trimOffspring", {"start": v(36.4, -21.71) * mm, "end": v(36.4, -27.05) * mm});
            skLineSegment(sketch, "E479.trimOffspring", {"start": v(30.04, -21.71) * mm, "end": v(30.04, -27.05) * mm});
            skLineSegment(sketch, "E480.trimOffspring", {"start": v(23.7, -21.71) * mm, "end": v(23.7, -27.05) * mm});
            skLineSegment(sketch, "E481.trimOffspring", {"start": v(17.34, -21.71) * mm, "end": v(17.34, -27.05) * mm});
            skLineSegment(sketch, "E482.trimOffspring", {"start": v(17.34, -15.36) * mm, "end": v(17.34, -20.7) * mm});
            skLineSegment(sketch, "E483.trimOffspring", {"start": v(23.7, -15.36) * mm, "end": v(23.7, -20.7) * mm});
            skLineSegment(sketch, "E484.trimOffspring", {"start": v(36.4, -15.36) * mm, "end": v(36.4, -20.7) * mm});
            skLineSegment(sketch, "E485.trimOffspring", {"start": v(23.7, -9.01) * mm, "end": v(23.7, -14.35) * mm});
            skLineSegment(sketch, "E486.trimOffspring", {"start": v(11, -28.06) * mm, "end": v(11, -33.4) * mm});
            skLineSegment(sketch, "E487.trimOffspring", {"start": v(17.34, -28.06) * mm, "end": v(17.34, -33.4) * mm});
            skLineSegment(sketch, "E488.trimOffspring", {"start": v(4.64, -28.06) * mm, "end": v(4.64, -33.4) * mm});
            skLineSegment(sketch, "E489", {"start": v(36.4, -8) * mm, "end": v(36.4, -2.66) * mm});
            skLineSegment(sketch, "E490.trimOffspring", {"start": v(42.74, -9.01) * mm, "end": v(42.74, -14.35) * mm});
            skLineSegment(sketch, "E491.trimOffspring", {"start": v(42.74, -15.36) * mm, "end": v(42.74, -20.7) * mm});
            skLineSegment(sketch, "E492.trimOffspring", {"start": v(42.74, -33.4) * mm, "end": v(46.28, -33.4) * mm});
            skPoint(sketch, "E493.orphan", {"position": v(42.74, -34.16) * mm});
            skLineSegment(sketch, "E494.trimOffspring", {"start": v(36.4, -33.4) * mm, "end": v(41.73, -33.4) * mm});
            skPoint(sketch, "E495.orphan", {"position": v(36.4, -34.16) * mm});
            skLineSegment(sketch, "E496.trimOffspring", {"start": v(30.04, -33.4) * mm, "end": v(35.38, -33.4) * mm});
            skLineSegment(sketch, "E497.trimOffspring", {"start": v(30.04, -34.16) * mm, "end": v(30.04, -34.41) * mm});
            skLineSegment(sketch, "E498.trimOffspring", {"start": v(23.7, -33.4) * mm, "end": v(29.03, -33.4) * mm});
            skPoint(sketch, "E499.orphan", {"position": v(23.7, -34.16) * mm});
            skLineSegment(sketch, "E500.trimOffspring", {"start": v(46.78, -9.01) * mm, "end": v(46.78, -20.7) * mm});
            skLineSegment(sketch, "E501.trimOffspring", {"start": v(42.74, -28.06) * mm, "end": v(42.74, -33.4) * mm});
            skLineSegment(sketch, "E502.trimOffspring", {"start": v(36.4, -34.16) * mm, "end": v(36.4, -34.41) * mm});
            skLineSegment(sketch, "E503.trimOffspring", {"start": v(23.7, -34.16) * mm, "end": v(23.7, -34.41) * mm});
            skLineSegment(sketch, "E504.trimOffspring", {"start": v(17.34, -33.4) * mm, "end": v(22.68, -33.4) * mm});
            skPoint(sketch, "E505.orphan", {"position": v(17.34, -34.16) * mm});
            skLineSegment(sketch, "E506.trimOffspring", {"start": v(42.74, -33.4) * mm, "end": v(46.78, -33.4) * mm});
            skLineSegment(sketch, "E507.trimOffspring", {"start": v(42.74, -34.16) * mm, "end": v(42.74, -34.41) * mm});
            skLineSegment(sketch, "E508.trimOffspring", {"start": v(17.34, -34.16) * mm, "end": v(17.34, -34.41) * mm});
            skLineSegment(sketch, "E509.trimOffspring", {"start": v(42.74, -21.71) * mm, "end": v(42.74, -27.05) * mm});
            skLineSegment(sketch, "E510.trimOffspring", {"start": v(46.78, -21.71) * mm, "end": v(46.78, -27.05) * mm});
            skLineSegment(sketch, "E511.trimOffspring", {"start": v(9.98, -34.41) * mm, "end": v(47.3, -34.41) * mm});
            skPoint(sketch, "E512.orphan", {"position": v(11, -34.16) * mm});
            skLineSegment(sketch, "E513.trimOffspring", {"start": v(4.64, -33.4) * mm, "end": v(16.33, -33.4) * mm});
            skPoint(sketch, "E514.orphan", {"position": v(4.64, -34.16) * mm});
            skLineSegment(sketch, "E515.trimOffspring", {"start": v(42.74, -33.4) * mm, "end": v(46.53, -33.4) * mm});
            skLineSegment(sketch, "E516.trimOffspring", {"start": v(46.78, -28.06) * mm, "end": v(46.78, -33.4) * mm});
            skLineSegment(sketch, "E517.trimOffspring", {"start": v(47.3, -28.06) * mm, "end": v(47.55, -28.06) * mm});
            skLineSegment(sketch, "E518.trimOffspring", {"start": v(-1.7, -33.4) * mm, "end": v(3.63, -33.4) * mm});
            skPoint(sketch, "E519.orphan", {"position": v(-1.7, -34.16) * mm});
            skLineSegment(sketch, "E520.trimOffspring", {"start": v(-8.06, -33.4) * mm, "end": v(-2.72, -33.4) * mm});
            skLineSegment(sketch, "E521.trimOffspring", {"start": v(-8.06, -34.16) * mm, "end": v(-8.06, -34.41) * mm});
            skLineSegment(sketch, "E522.trimOffspring", {"start": v(-1.7, -28.06) * mm, "end": v(-1.7, -33.4) * mm});
            skLineSegment(sketch, "E523.trimOffspring", {"start": v(-1.7, -34.16) * mm, "end": v(-1.7, -34.41) * mm});
            skLineSegment(sketch, "E524.trimOffspring", {"start": v(-14.4, -33.4) * mm, "end": v(-9.07, -33.4) * mm});
            skPoint(sketch, "E525.orphan", {"position": v(-14.4, -34.16) * mm});
            skLineSegment(sketch, "E526.trimOffspring", {"start": v(-14.4, -28.06) * mm, "end": v(-14.4, -33.4) * mm});
            skLineSegment(sketch, "E527.trimOffspring", {"start": v(-8.06, -28.06) * mm, "end": v(-8.06, -33.4) * mm});
            skLineSegment(sketch, "E528.trimOffspring", {"start": v(-20.76, -21.71) * mm, "end": v(-20.76, -27.05) * mm});
            skLineSegment(sketch, "E529.trimOffspring", {"start": v(4.64, -33.4) * mm, "end": v(9.98, -33.4) * mm});
            skLineSegment(sketch, "E530.trimOffspring", {"start": v(4.64, -34.16) * mm, "end": v(4.64, -34.41) * mm});
            skLineSegment(sketch, "E531.trimOffspring", {"start": v(11, -34.16) * mm, "end": v(11, -34.41) * mm});
            skLineSegment(sketch, "E532.trimOffspring", {"start": v(-14.4, -34.16) * mm, "end": v(-14.4, -34.41) * mm});
            skLineSegment(sketch, "E533.trimOffspring", {"start": v(-1.7, -33.4) * mm, "end": v(16.33, -33.4) * mm});
            skLineSegment(sketch, "E534.trimOffspring", {"start": v(11, -33.4) * mm, "end": v(16.33, -33.4) * mm});
            skLineSegment(sketch, "E535.trimOffspring", {"start": v(-39.8, -28.06) * mm, "end": v(-39.8, -33.4) * mm});
            skLineSegment(sketch, "E536.trimOffspring", {"start": v(-46.16, -28.06) * mm, "end": v(-46.16, -33.4) * mm});
            skLineSegment(sketch, "E537.trimOffspring", {"start": v(-52.5, -28.06) * mm, "end": v(-52.5, -33.4) * mm});
            skLineSegment(sketch, "E538.trimOffspring", {"start": v(-58.86, -28.06) * mm, "end": v(-58.86, -34.16) * mm});
            skLineSegment(sketch, "E539.trimOffspring", {"start": v(-58.86, -21.71) * mm, "end": v(-58.86, -27.05) * mm});
            skLineSegment(sketch, "E540.trimOffspring", {"start": v(-52.5, -21.71) * mm, "end": v(-52.5, -27.05) * mm});
            skLineSegment(sketch, "E541.trimOffspring", {"start": v(-46.16, -21.71) * mm, "end": v(-46.16, -27.05) * mm});
            skLineSegment(sketch, "E542.trimOffspring", {"start": v(-39.8, -21.71) * mm, "end": v(-39.8, -27.05) * mm});
            skLineSegment(sketch, "E543.trimOffspring", {"start": v(-33.46, -21.71) * mm, "end": v(-33.46, -27.05) * mm});
            skLineSegment(sketch, "E544.trimOffspring", {"start": v(-27.1, -15.36) * mm, "end": v(-27.1, -20.7) * mm});
            skLineSegment(sketch, "E545.trimOffspring", {"start": v(-33.46, -15.36) * mm, "end": v(-33.46, -20.7) * mm});
            skLineSegment(sketch, "E546.trimOffspring", {"start": v(-46.16, -15.36) * mm, "end": v(-46.16, -20.7) * mm});
            skLineSegment(sketch, "E547.trimOffspring", {"start": v(-52.5, -15.36) * mm, "end": v(-52.5, -20.7) * mm});
            skLineSegment(sketch, "E548.trimOffspring", {"start": v(-58.86, -15.36) * mm, "end": v(-58.86, -20.7) * mm});
            skLineSegment(sketch, "E549.trimOffspring", {"start": v(-58.86, -9.01) * mm, "end": v(-58.86, -14.35) * mm});
            skLineSegment(sketch, "E550.trimOffspring", {"start": v(-52.5, -9.01) * mm, "end": v(-52.5, -14.35) * mm});
            skLineSegment(sketch, "E551.trimOffspring", {"start": v(-46.16, -9.01) * mm, "end": v(-46.16, -14.35) * mm});
            skLineSegment(sketch, "E552.trimOffspring", {"start": v(-39.8, -9.01) * mm, "end": v(-39.8, -14.35) * mm});
            skLineSegment(sketch, "E553.trimOffspring", {"start": v(-33.46, -9.01) * mm, "end": v(-33.46, -14.35) * mm});
            skPoint(sketch, "E554.orphan", {"position": v(-39.8, -34.16) * mm});
            skLineSegment(sketch, "E555.trimOffspring", {"start": v(-46.16, -34.16) * mm, "end": v(-46.16, -34.41) * mm});
            skPoint(sketch, "E556.orphan", {"position": v(-52.5, -34.16) * mm});
            skLineSegment(sketch, "E557.trimOffspring", {"start": v(-27.1, -33.4) * mm, "end": v(-20.76, -33.4) * mm});
            skLineSegment(sketch, "E558.trimOffspring", {"start": v(-33.46, -33.4) * mm, "end": v(-15.42, -33.4) * mm});
            skLineSegment(sketch, "E559.trimOffspring", {"start": v(-39.8, -34.16) * mm, "end": v(-39.8, -34.41) * mm});
            skLineSegment(sketch, "E560.trimOffspring", {"start": v(-39.8, -33.4) * mm, "end": v(-34.47, -33.4) * mm});
            skLineSegment(sketch, "E561.trimOffspring", {"start": v(-46.16, -33.4) * mm, "end": v(-40.82, -33.4) * mm});
            skLineSegment(sketch, "E562.trimOffspring", {"start": v(-52.5, -34.16) * mm, "end": v(-52.5, -34.41) * mm});
            skLineSegment(sketch, "E563.trimOffspring", {"start": v(-52.5, -33.4) * mm, "end": v(-47.17, -33.4) * mm});
            skLineSegment(sketch, "E564.trimOffspring", {"start": v(-20.76, -28.06) * mm, "end": v(-20.76, -34.16) * mm});
            skLineSegment(sketch, "E565.trimOffspring", {"start": v(-27.1, -28.06) * mm, "end": v(-27.1, -33.4) * mm});
            skLineSegment(sketch, "E566.trimOffspring", {"start": v(-20.76, -34.16) * mm, "end": v(-20.76, -34.41) * mm});
            skLineSegment(sketch, "E567.trimOffspring", {"start": v(-52.5, -33.4) * mm, "end": v(-34.47, -33.4) * mm});
            skLineSegment(sketch, "E568.trimOffspring", {"start": v(-33.46, -33.4) * mm, "end": v(-14.4, -33.4) * mm});
            skLineSegment(sketch, "E569.trimOffspring", {"start": v(-15.42, -15.36) * mm, "end": v(-15.42, -34.16) * mm});
            skLineSegment(sketch, "E570.trimOffspring", {"start": v(-27.1, 3.69) * mm, "end": v(-27.1, -1.65) * mm});
            skLineSegment(sketch, "E571.trimOffspring", {"start": v(-39.8, 3.69) * mm, "end": v(-39.8, -1.65) * mm});
            skLineSegment(sketch, "E572.trimOffspring", {"start": v(-46.16, 3.69) * mm, "end": v(-46.16, -1.65) * mm});
            skLineSegment(sketch, "E573.trimOffspring", {"start": v(-52.5, 3.69) * mm, "end": v(-52.5, -1.65) * mm});
            skLineSegment(sketch, "E574.trimOffspring", {"start": v(-52.5, 10.04) * mm, "end": v(-52.5, 4.7) * mm});
            skLineSegment(sketch, "E575.trimOffspring", {"start": v(-39.8, 10.04) * mm, "end": v(-39.8, 4.7) * mm});
            skLineSegment(sketch, "E576.trimOffspring", {"start": v(-33.46, 10.04) * mm, "end": v(-33.46, 4.7) * mm});
            skLineSegment(sketch, "E577.trimOffspring", {"start": v(-27.1, 10.04) * mm, "end": v(-27.1, 4.7) * mm});
            skLineSegment(sketch, "E578.trimOffspring", {"start": v(-20.76, 10.04) * mm, "end": v(-20.76, 4.7) * mm});
            skLineSegment(sketch, "E579.trimOffspring", {"start": v(-14.4, 10.04) * mm, "end": v(-14.4, 4.7) * mm});
            skLineSegment(sketch, "E580.trimOffspring", {"start": v(-33.46, -2.66) * mm, "end": v(-33.46, -8) * mm});
            skLineSegment(sketch, "E581.trimOffspring", {"start": v(-39.8, -2.66) * mm, "end": v(-39.8, -8) * mm});
            skLineSegment(sketch, "E582.trimOffspring", {"start": v(-65.2, -2.66) * mm, "end": v(-65.2, -8) * mm});
            skLineSegment(sketch, "E583.trimOffspring", {"start": v(-65.2, 3.69) * mm, "end": v(-65.2, -1.65) * mm});
            skLineSegment(sketch, "E584.trimOffspring", {"start": v(-65.2, 10.04) * mm, "end": v(-65.2, 4.7) * mm});
            skLineSegment(sketch, "E585.trimOffspring", {"start": v(-46.16, -2.66) * mm, "end": v(-46.16, -8) * mm});
            skLineSegment(sketch, "E586.trimOffspring", {"start": v(-52.5, -2.66) * mm, "end": v(-52.5, -8) * mm});
            skLineSegment(sketch, "E587.trimOffspring", {"start": v(-58.86, 10.04) * mm, "end": v(-58.86, 4.7) * mm});
            skLineSegment(sketch, "E588.trimOffspring", {"start": v(-8.06, 10.04) * mm, "end": v(-8.06, 4.7) * mm});
            skLineSegment(sketch, "E589", {"start": v(-58.86, -8) * mm, "end": v(-58.86, -2.66) * mm});
            skLineSegment(sketch, "E590", {"start": v(-27.1, -2.66) * mm, "end": v(-27.1, -8) * mm});
            skLineSegment(sketch, "E591.trimOffspring", {"start": v(-65.2, -28.06) * mm, "end": v(-65.2, -34.16) * mm});
            skLineSegment(sketch, "E592.trimOffspring", {"start": v(-65.2, -21.71) * mm, "end": v(-65.2, -27.05) * mm});
            skLineSegment(sketch, "E593.trimOffspring", {"start": v(-65.2, -15.36) * mm, "end": v(-65.2, -20.7) * mm});
            skLineSegment(sketch, "E594.trimOffspring", {"start": v(-65.2, -9.01) * mm, "end": v(-65.2, -14.35) * mm});
            skPoint(sketch, "E595.orphan", {"position": v(-59.87, -34.16) * mm});
            skLineSegment(sketch, "E596.trimOffspring", {"start": v(-65.2, 16.39) * mm, "end": v(-65.2, 11.05) * mm});
            skLineSegment(sketch, "E597.trimOffspring", {"start": v(-52.5, 16.39) * mm, "end": v(-52.5, 11.05) * mm});
            skLineSegment(sketch, "E598.trimOffspring", {"start": v(-33.46, 16.39) * mm, "end": v(-33.46, 11.05) * mm});
            skLineSegment(sketch, "E599.trimOffspring", {"start": v(-27.1, 16.39) * mm, "end": v(-27.1, 11.05) * mm});
            skLineSegment(sketch, "E600.trimOffspring", {"start": v(-20.76, 16.39) * mm, "end": v(-20.76, 11.05) * mm});
            skLineSegment(sketch, "E601.trimOffspring", {"start": v(-58.86, 16.39) * mm, "end": v(-58.86, 11.05) * mm});
            skLineSegment(sketch, "E602.trimOffspring", {"start": v(-46.16, 16.39) * mm, "end": v(-46.16, 11.05) * mm});
            skLineSegment(sketch, "E603", {"start": v(-20.76, -20.7) * mm, "end": v(-20.76, -15.36) * mm});
            skLineSegment(sketch, "E604.trimOffspring", {"start": v(-9.07, -15.36) * mm, "end": v(-9.07, -34.16) * mm});
            skLineSegment(sketch, "E605", {"start": v(-9.07, -9.01) * mm, "end": v(-9.07, -14.35) * mm});
            skLineSegment(sketch, "E606.trimOffspring", {"start": v(-21.77, 3.69) * mm, "end": v(-21.77, -8) * mm});
            skLineSegment(sketch, "E607.trimOffspring", {"start": v(-28.12, 3.69) * mm, "end": v(-28.12, -2.66) * mm});
            skLineSegment(sketch, "E608.trimOffspring", {"start": v(-40.82, 3.69) * mm, "end": v(-40.82, -34.16) * mm});
            skLineSegment(sketch, "E609.trimOffspring", {"start": v(-47.17, 3.69) * mm, "end": v(-47.17, -34.16) * mm});
            skLineSegment(sketch, "E610.trimOffspring", {"start": v(-28.12, 3.69) * mm, "end": v(-28.12, -34.16) * mm});
            skLineSegment(sketch, "E611.trimOffspring", {"start": v(-21.77, 3.69) * mm, "end": v(-21.77, -34.16) * mm});
            skLineSegment(sketch, "E612.trimOffspring", {"start": v(-59.87, 3.69) * mm, "end": v(-59.87, -8) * mm});
            skLineSegment(sketch, "E613.trimOffspring", {"start": v(-66.22, 3.69) * mm, "end": v(-66.22, -1.65) * mm});
            skLineSegment(sketch, "E614", {"start": v(-21.77, 10.04) * mm, "end": v(-21.77, 4.7) * mm});
            skLineSegment(sketch, "E615", {"start": v(-28.12, 4.7) * mm, "end": v(-28.12, 10.04) * mm});
            skLineSegment(sketch, "E616", {"start": v(-53.52, 4.7) * mm, "end": v(-53.52, 10.04) * mm});
            skLineSegment(sketch, "E617.trimOffspring", {"start": v(-59.87, -9.01) * mm, "end": v(-59.87, -33.4) * mm});
            skLineSegment(sketch, "E618.trimOffspring", {"start": v(-59.87, -9.01) * mm, "end": v(-59.87, -14.35) * mm});
            skLineSegment(sketch, "E619.trimOffspring", {"start": v(42.74, 16.39) * mm, "end": v(42.74, 11.05) * mm});
            skLineSegment(sketch, "E620.trimOffspring", {"start": v(35.38, 10.04) * mm, "end": v(35.38, -34.16) * mm});
            skLineSegment(sketch, "E621.trimOffspring", {"start": v(41.73, 10.04) * mm, "end": v(41.73, -34.16) * mm});
            skLineSegment(sketch, "E622.trimOffspring", {"start": v(41.73, 10.04) * mm, "end": v(41.73, -34.41) * mm});
            skLineSegment(sketch, "E623.trimOffspring", {"start": v(47.55, 10.04) * mm, "end": v(47.3, 10.04) * mm});
            skPoint(sketch, "E624.orphan", {"position": v(47.8, 10.04) * mm});
            skPoint(sketch, "E625.orphan", {"position": v(47.8, 3.69) * mm});
            skPoint(sketch, "E626.orphan", {"position": v(47.8, -2.66) * mm});
            skPoint(sketch, "E627.orphan", {"position": v(47.8, -9.01) * mm});
            skPoint(sketch, "E628.orphan", {"position": v(47.8, -15.36) * mm});
            skPoint(sketch, "E629.orphan", {"position": v(47.8, -28.06) * mm});
            skPoint(sketch, "E630.orphan", {"position": v(47.8, -21.71) * mm});
            skPoint(sketch, "E631.orphan", {"position": v(35.38, -34.41) * mm});
            skPoint(sketch, "E632.orphan", {"position": v(22.68, -34.41) * mm});
            skPoint(sketch, "E633.orphan", {"position": v(16.33, -34.41) * mm});
            skPoint(sketch, "E634.orphan", {"position": v(-2.72, -34.41) * mm});
            skPoint(sketch, "E635.orphan", {"position": v(3.63, -34.41) * mm});
            skPoint(sketch, "E636.orphan", {"position": v(-9.07, -34.41) * mm});
            skPoint(sketch, "E637.orphan", {"position": v(-15.42, -34.41) * mm});
            skPoint(sketch, "E638.orphan", {"position": v(-21.77, -34.41) * mm});
            skPoint(sketch, "E639.orphan", {"position": v(-28.12, -34.41) * mm});
            skPoint(sketch, "E640.orphan", {"position": v(-34.47, -34.41) * mm});
            skPoint(sketch, "E641.orphan", {"position": v(-40.82, -34.41) * mm});
            skPoint(sketch, "E642.orphan", {"position": v(-47.17, -34.41) * mm});
            skPoint(sketch, "E643.orphan", {"position": v(-53.52, -34.41) * mm});
            skPoint(sketch, "E644.orphan", {"position": v(-58.86, -34.41) * mm});
            skLineSegment(sketch, "E645.trimOffspring", {"start": v(-59.87, -34.16) * mm, "end": v(-59.87, -34.41) * mm});
            skPoint(sketch, "E646.orphan", {"position": v(-65.2, -34.41) * mm});
            skLineSegment(sketch, "E647.trimOffspring", {"start": v(-71.56, -15.36) * mm, "end": v(-66.22, -15.36) * mm});
            skLineSegment(sketch, "E648.trimOffspring", {"start": v(-71.56, -21.71) * mm, "end": v(-71.56, -33.4) * mm});
            skLineSegment(sketch, "E649.trimOffspring", {"start": v(-59.87, -21.71) * mm, "end": v(-59.87, -33.4) * mm});
            skLineSegment(sketch, "E650", {"start": v(-71.56, -20.7) * mm, "end": v(-71.56, -15.36) * mm});
            skLineSegment(sketch, "E651.trimOffspring", {"start": v(-21.77, -28.06) * mm, "end": v(-21.77, -34.16) * mm});
            skLineSegment(sketch, "E652.trimOffspring", {"start": v(-1.7, 21) * mm, "end": v(-1.7, 17.4) * mm});
            skLineSegment(sketch, "E653.trimOffspring", {"start": v(-14.4, 21) * mm, "end": v(-14.4, 17.4) * mm});
            skLineSegment(sketch, "E654", {"start": v(-20.76, 21) * mm, "end": v(-20.76, 17.4) * mm});
            skLineSegment(sketch, "E655.trimOffspring", {"start": v(-27.1, -28.06) * mm, "end": v(-27.1, -34.16) * mm});
            skLineSegment(sketch, "E656", {"start": v(-27.1, -27.05) * mm, "end": v(-27.1, -21.71) * mm});
            skLineSegment(sketch, "E657", {"start": v(-27.1, -14.35) * mm, "end": v(-27.1, -9.01) * mm});
            skLineSegment(sketch, "E658.trimOffspring", {"start": v(-66.22, -28.06) * mm, "end": v(-66.22, -34.16) * mm});
            skLineSegment(sketch, "E659.trimOffspring", {"start": v(-66.22, -9.01) * mm, "end": v(-66.22, -14.35) * mm});
            skLineSegment(sketch, "E660.trimOffspring", {"start": v(-66.22, -15.36) * mm, "end": v(-66.22, -20.7) * mm});
            skLineSegment(sketch, "E661.trimOffspring", {"start": v(-66.22, -21.71) * mm, "end": v(-66.22, -27.05) * mm});
            skLineSegment(sketch, "E662.trimOffspring", {"start": v(-66.22, -2.66) * mm, "end": v(-66.22, -8) * mm});
            skLineSegment(sketch, "E663.trimOffspring", {"start": v(-66.22, 10.04) * mm, "end": v(-66.22, 4.7) * mm});
            skLineSegment(sketch, "E664.trimOffspring", {"start": v(-71.56, 10.04) * mm, "end": v(-71.56, -15.36) * mm});
            skLineSegment(sketch, "E665.trimOffspring", {"start": v(-71.56, 10.04) * mm, "end": v(-66.22, 10.04) * mm});
            skLineSegment(sketch, "E666", {"start": v(-71.56, 11.05) * mm, "end": v(-71.56, 16.39) * mm});
            skLineSegment(sketch, "E667.trimOffspring", {"start": v(-65.2, 21) * mm, "end": v(-65.2, 17.4) * mm});
            skLineSegment(sketch, "E668.trimOffspring", {"start": v(-39.8, 21) * mm, "end": v(-39.8, 17.4) * mm});
            skPoint(sketch, "E669.orphan", {"position": v(-72.57, 3.69) * mm});
            skLineSegment(sketch, "E670.trimOffspring", {"start": v(-66.22, 16.39) * mm, "end": v(-66.22, 11.05) * mm});
            skLineSegment(sketch, "E671", {"start": v(-66.22, 17.4) * mm, "end": v(-66.22, 21) * mm});
            skLineSegment(sketch, "E672.trimOffspring", {"start": v(-14.4, 21) * mm, "end": v(-9.07, 21) * mm});
            skLineSegment(sketch, "E673.trimOffspring", {"start": v(-33.46, 21) * mm, "end": v(-33.46, 17.4) * mm});
            skLineSegment(sketch, "E674.trimOffspring", {"start": v(-27.1, 21) * mm, "end": v(-27.1, 17.4) * mm});
            skLineSegment(sketch, "E675.trimOffspring", {"start": v(-28.12, 21) * mm, "end": v(-28.12, 10.04) * mm});
            skLineSegment(sketch, "E676", {"start": v(-34.47, 20.97) * mm, "end": v(-39.8, 21) * mm});
            skSolve(sketch);
        }
        {
            var Q0;
            {var subQ0=sQuery(id+"F11.wireOp",EDGE,"E194.trimOffspring");Q0=makeQuery(id+"F11.imprint","IMPRINT",FACE,{"disambiguationData":[TD([[makeQuery(id+"F11.imprint","IMPRINT",EDGE,{"derivedFrom":subQ0}),1.0]])]});}
            var Q1;
            {var subQ269=sQuery(id+"F11.wireOp",EDGE,"E35.top");Q1=makeQuery(id+"F11.imprint","IMPRINT",FACE,{"disambiguationData":[TD([[makeQuery(id+"F11.imprint","IMPRINT",EDGE,{"derivedFrom":subQ269}),1.0]])]});}
            var Q2;
            Q2=makeQuery(id+"F6.opExtrude","SWEPT_FACE",FACE,{"disambiguationData":[OSD([sQuery(id+"F5.wireOp",EDGE,"E9")])]});
            extrude(context, id + "F12", {"entities" : qUnion([Q0, Q1, Q2]), "operationType" : NewBodyOperationType.ADD, "oppositeDirection" : true, "depth" : 1.52 * mm});
        }
    });
